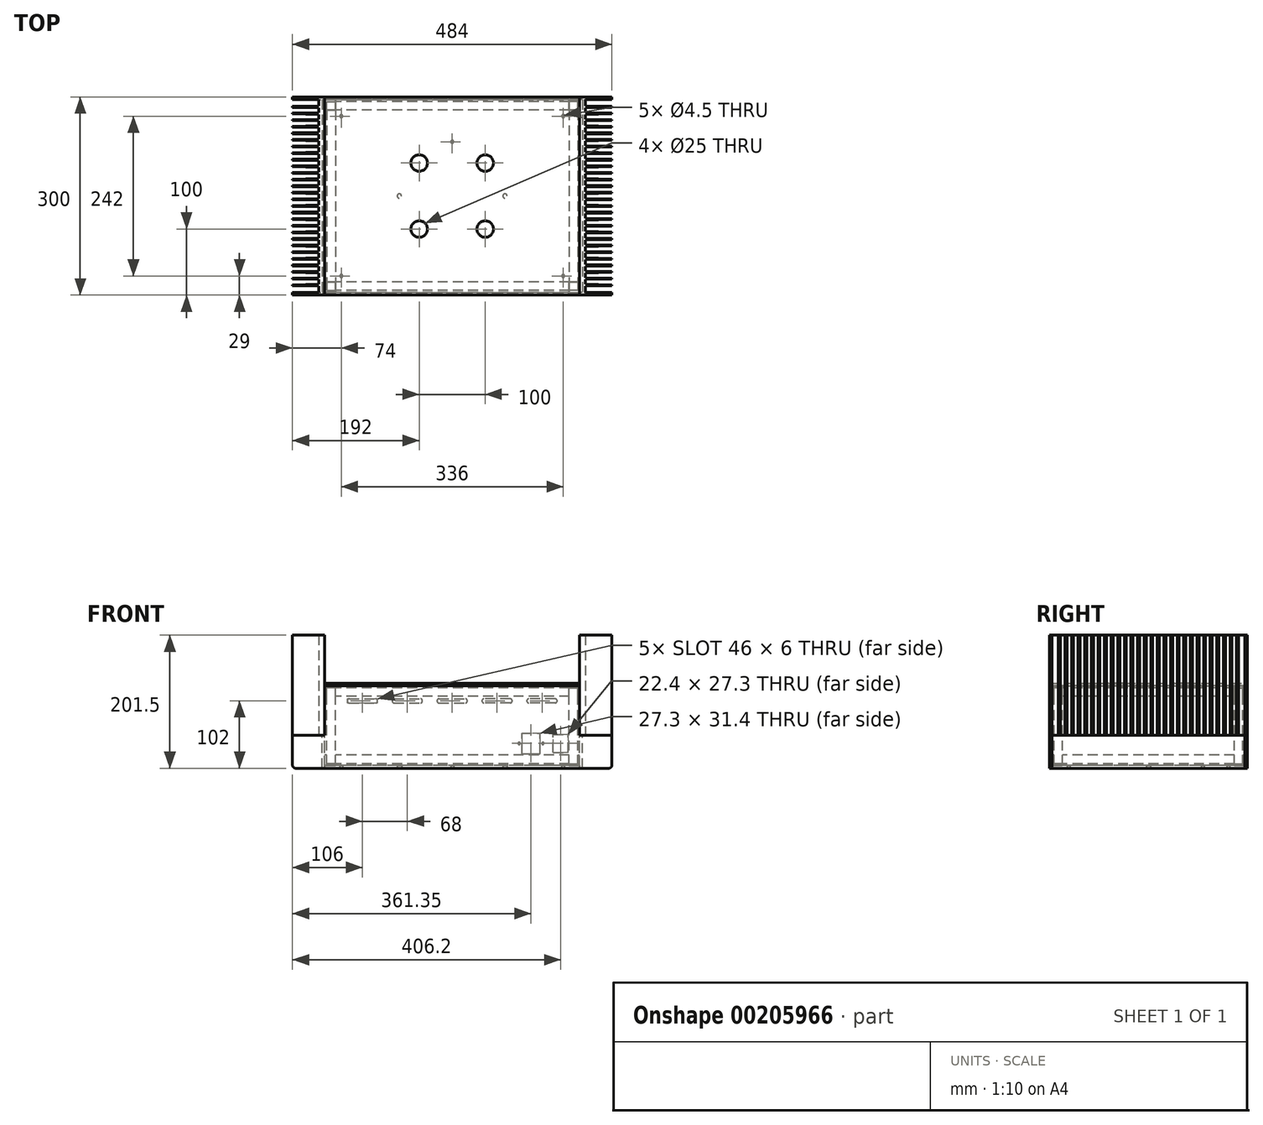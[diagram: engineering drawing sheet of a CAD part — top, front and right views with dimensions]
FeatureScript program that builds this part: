
annotation { "Feature Type Name" : "Feature", "Feature Type Description" : "" }
export const myFeature = defineFeature(function(context is Context, id is Id, definition is map)
    precondition{}
    {
        {
            var Q0;
            Q0=qCreatedBy(makeId("Top.planeOp"),FACE);
            var sketch = newSketch(context, id + "F0", { "sketchPlane" : qUnion([Q0])});
            skLineSegment(sketch, "E0", {"start": v(0, 0) * mm, "end": v(11.17, 0) * mm, "construction": true});
            skLineSegment(sketch, "E1", {"start": v(0, 0) * mm, "end": v(0, 12.82) * mm, "construction": true});
            skLineSegment(sketch, "E2", {"start": v(0, 49) * mm, "end": v(0.75, 49) * mm});
            skLineSegment(sketch, "E3", {"start": v(0.75, 49) * mm, "end": v(1.5, 9) * mm});
            skLineSegment(sketch, "E4", {"start": v(1.5, 9) * mm, "end": v(8.5, 9) * mm});
            skLineSegment(sketch, "E5", {"start": v(8.5, 9) * mm, "end": v(9.25, 49) * mm});
            skLineSegment(sketch, "E6", {"start": v(5, 24.61) * mm, "end": v(5, 0) * mm, "construction": true});
            skPoint(sketch, "E6.startSnap0", {"position": v(5, 9) * mm});
            skLineSegment(sketch, "E7", {"start": v(9.25, 49) * mm, "end": v(10, 49) * mm});
            skLineSegment(sketch, "E8.1.0.0", {"start": v(11.5, 9) * mm, "end": v(18.5, 9) * mm});
            skLineSegment(sketch, "E8.1.0.1", {"start": v(18.5, 9) * mm, "end": v(19.25, 49) * mm});
            skLineSegment(sketch, "E8.1.0.2", {"start": v(10.75, 49) * mm, "end": v(11.5, 9) * mm});
            skPoint(sketch, "E8.1.0.3", {"position": v(15, 9) * mm});
            skLineSegment(sketch, "E8.1.0.4", {"start": v(10, 49) * mm, "end": v(10.75, 49) * mm});
            skLineSegment(sketch, "E8.1.0.5", {"start": v(19.25, 49) * mm, "end": v(20, 49) * mm});
            skLineSegment(sketch, "E8.2.0.0", {"start": v(21.5, 9) * mm, "end": v(28.5, 9) * mm});
            skLineSegment(sketch, "E8.2.0.1", {"start": v(28.5, 9) * mm, "end": v(29.25, 49) * mm});
            skLineSegment(sketch, "E8.2.0.2", {"start": v(20.75, 49) * mm, "end": v(21.5, 9) * mm});
            skPoint(sketch, "E8.2.0.3", {"position": v(25, 9) * mm});
            skLineSegment(sketch, "E8.2.0.4", {"start": v(20, 49) * mm, "end": v(20.75, 49) * mm});
            skLineSegment(sketch, "E8.2.0.5", {"start": v(29.25, 49) * mm, "end": v(30, 49) * mm});
            skLineSegment(sketch, "E8.3.0.0", {"start": v(31.5, 9) * mm, "end": v(38.5, 9) * mm});
            skLineSegment(sketch, "E8.3.0.1", {"start": v(38.5, 9) * mm, "end": v(39.25, 49) * mm});
            skLineSegment(sketch, "E8.3.0.2", {"start": v(30.75, 49) * mm, "end": v(31.5, 9) * mm});
            skPoint(sketch, "E8.3.0.3", {"position": v(35, 9) * mm});
            skLineSegment(sketch, "E8.3.0.4", {"start": v(30, 49) * mm, "end": v(30.75, 49) * mm});
            skLineSegment(sketch, "E8.3.0.5", {"start": v(39.25, 49) * mm, "end": v(40, 49) * mm});
            skLineSegment(sketch, "E8.4.0.0", {"start": v(41.5, 9) * mm, "end": v(48.5, 9) * mm});
            skLineSegment(sketch, "E8.4.0.1", {"start": v(48.5, 9) * mm, "end": v(49.25, 49) * mm});
            skLineSegment(sketch, "E8.4.0.2", {"start": v(40.75, 49) * mm, "end": v(41.5, 9) * mm});
            skPoint(sketch, "E8.4.0.3", {"position": v(45, 9) * mm});
            skLineSegment(sketch, "E8.4.0.4", {"start": v(40, 49) * mm, "end": v(40.75, 49) * mm});
            skLineSegment(sketch, "E8.4.0.5", {"start": v(49.25, 49) * mm, "end": v(50, 49) * mm});
            skLineSegment(sketch, "E8.5.0.0", {"start": v(51.5, 9) * mm, "end": v(58.5, 9) * mm});
            skLineSegment(sketch, "E8.5.0.1", {"start": v(58.5, 9) * mm, "end": v(59.25, 49) * mm});
            skLineSegment(sketch, "E8.5.0.2", {"start": v(50.75, 49) * mm, "end": v(51.5, 9) * mm});
            skPoint(sketch, "E8.5.0.3", {"position": v(55, 9) * mm});
            skLineSegment(sketch, "E8.5.0.4", {"start": v(50, 49) * mm, "end": v(50.75, 49) * mm});
            skLineSegment(sketch, "E8.5.0.5", {"start": v(59.25, 49) * mm, "end": v(60, 49) * mm});
            skLineSegment(sketch, "E8.6.0.0", {"start": v(61.5, 9) * mm, "end": v(68.5, 9) * mm});
            skLineSegment(sketch, "E8.6.0.1", {"start": v(68.5, 9) * mm, "end": v(69.25, 49) * mm});
            skLineSegment(sketch, "E8.6.0.2", {"start": v(60.75, 49) * mm, "end": v(61.5, 9) * mm});
            skPoint(sketch, "E8.6.0.3", {"position": v(65, 9) * mm});
            skLineSegment(sketch, "E8.6.0.4", {"start": v(60, 49) * mm, "end": v(60.75, 49) * mm});
            skLineSegment(sketch, "E8.6.0.5", {"start": v(69.25, 49) * mm, "end": v(70, 49) * mm});
            skLineSegment(sketch, "E8.7.0.0", {"start": v(71.5, 9) * mm, "end": v(78.5, 9) * mm});
            skLineSegment(sketch, "E8.7.0.1", {"start": v(78.5, 9) * mm, "end": v(79.25, 49) * mm});
            skLineSegment(sketch, "E8.7.0.2", {"start": v(70.75, 49) * mm, "end": v(71.5, 9) * mm});
            skPoint(sketch, "E8.7.0.3", {"position": v(75, 9) * mm});
            skLineSegment(sketch, "E8.7.0.4", {"start": v(70, 49) * mm, "end": v(70.75, 49) * mm});
            skLineSegment(sketch, "E8.7.0.5", {"start": v(79.25, 49) * mm, "end": v(80, 49) * mm});
            skLineSegment(sketch, "E8.8.0.0", {"start": v(81.5, 9) * mm, "end": v(88.5, 9) * mm});
            skLineSegment(sketch, "E8.8.0.1", {"start": v(88.5, 9) * mm, "end": v(89.25, 49) * mm});
            skLineSegment(sketch, "E8.8.0.2", {"start": v(80.75, 49) * mm, "end": v(81.5, 9) * mm});
            skPoint(sketch, "E8.8.0.3", {"position": v(85, 9) * mm});
            skLineSegment(sketch, "E8.8.0.4", {"start": v(80, 49) * mm, "end": v(80.75, 49) * mm});
            skLineSegment(sketch, "E8.8.0.5", {"start": v(89.25, 49) * mm, "end": v(90, 49) * mm});
            skLineSegment(sketch, "E8.9.0.0", {"start": v(91.5, 9) * mm, "end": v(98.5, 9) * mm});
            skLineSegment(sketch, "E8.9.0.1", {"start": v(98.5, 9) * mm, "end": v(99.25, 49) * mm});
            skLineSegment(sketch, "E8.9.0.2", {"start": v(90.75, 49) * mm, "end": v(91.5, 9) * mm});
            skPoint(sketch, "E8.9.0.3", {"position": v(95, 9) * mm});
            skLineSegment(sketch, "E8.9.0.4", {"start": v(90, 49) * mm, "end": v(90.75, 49) * mm});
            skLineSegment(sketch, "E8.9.0.5", {"start": v(99.25, 49) * mm, "end": v(100, 49) * mm});
            skLineSegment(sketch, "E8.10.0.0", {"start": v(101.5, 9) * mm, "end": v(108.5, 9) * mm});
            skLineSegment(sketch, "E8.10.0.1", {"start": v(108.5, 9) * mm, "end": v(109.25, 49) * mm});
            skLineSegment(sketch, "E8.10.0.2", {"start": v(100.75, 49) * mm, "end": v(101.5, 9) * mm});
            skPoint(sketch, "E8.10.0.3", {"position": v(105, 9) * mm});
            skLineSegment(sketch, "E8.10.0.4", {"start": v(100, 49) * mm, "end": v(100.75, 49) * mm});
            skLineSegment(sketch, "E8.10.0.5", {"start": v(109.25, 49) * mm, "end": v(110, 49) * mm});
            skLineSegment(sketch, "E8.11.0.0", {"start": v(111.5, 9) * mm, "end": v(118.5, 9) * mm});
            skLineSegment(sketch, "E8.11.0.1", {"start": v(118.5, 9) * mm, "end": v(119.25, 49) * mm});
            skLineSegment(sketch, "E8.11.0.2", {"start": v(110.75, 49) * mm, "end": v(111.5, 9) * mm});
            skPoint(sketch, "E8.11.0.3", {"position": v(115, 9) * mm});
            skLineSegment(sketch, "E8.11.0.4", {"start": v(110, 49) * mm, "end": v(110.75, 49) * mm});
            skLineSegment(sketch, "E8.11.0.5", {"start": v(119.25, 49) * mm, "end": v(120, 49) * mm});
            skLineSegment(sketch, "E8.12.0.0", {"start": v(121.5, 9) * mm, "end": v(128.5, 9) * mm});
            skLineSegment(sketch, "E8.12.0.1", {"start": v(128.5, 9) * mm, "end": v(129.25, 49) * mm});
            skLineSegment(sketch, "E8.12.0.2", {"start": v(120.75, 49) * mm, "end": v(121.5, 9) * mm});
            skPoint(sketch, "E8.12.0.3", {"position": v(125, 9) * mm});
            skLineSegment(sketch, "E8.12.0.4", {"start": v(120, 49) * mm, "end": v(120.75, 49) * mm});
            skLineSegment(sketch, "E8.12.0.5", {"start": v(129.25, 49) * mm, "end": v(130, 49) * mm});
            skLineSegment(sketch, "E8.13.0.0", {"start": v(131.5, 9) * mm, "end": v(138.5, 9) * mm});
            skLineSegment(sketch, "E8.13.0.1", {"start": v(138.5, 9) * mm, "end": v(139.25, 49) * mm});
            skLineSegment(sketch, "E8.13.0.2", {"start": v(130.75, 49) * mm, "end": v(131.5, 9) * mm});
            skPoint(sketch, "E8.13.0.3", {"position": v(135, 9) * mm});
            skLineSegment(sketch, "E8.13.0.4", {"start": v(130, 49) * mm, "end": v(130.75, 49) * mm});
            skLineSegment(sketch, "E8.13.0.5", {"start": v(139.25, 49) * mm, "end": v(140, 49) * mm});
            skLineSegment(sketch, "E8.14.0.2", {"start": v(140.75, 49) * mm, "end": v(141.5, 9) * mm});
            skLineSegment(sketch, "E8.14.0.4", {"start": v(140, 49) * mm, "end": v(140.75, 49) * mm});
            skLineSegment(sketch, "E8.direction1", {"start": v(1.5, 9) * mm, "end": v(11.5, 9) * mm, "construction": true});
            skLineSegment(sketch, "E9.1.0.0", {"start": v(-9.25, 49) * mm, "end": v(-8.5, 9) * mm});
            skLineSegment(sketch, "E9.1.0.1", {"start": v(-8.5, 9) * mm, "end": v(-1.5, 9) * mm});
            skLineSegment(sketch, "E9.1.0.2", {"start": v(-1.5, 9) * mm, "end": v(-0.75, 49) * mm});
            skPoint(sketch, "E9.1.0.3", {"position": v(-5, 9) * mm});
            skLineSegment(sketch, "E9.1.0.4", {"start": v(-10, 49) * mm, "end": v(-9.25, 49) * mm});
            skLineSegment(sketch, "E9.1.0.5", {"start": v(-0.75, 49) * mm, "end": v(0, 49) * mm});
            skLineSegment(sketch, "E9.2.0.0", {"start": v(-19.25, 49) * mm, "end": v(-18.5, 9) * mm});
            skLineSegment(sketch, "E9.2.0.1", {"start": v(-18.5, 9) * mm, "end": v(-11.5, 9) * mm});
            skLineSegment(sketch, "E9.2.0.2", {"start": v(-11.5, 9) * mm, "end": v(-10.75, 49) * mm});
            skPoint(sketch, "E9.2.0.3", {"position": v(-15, 9) * mm});
            skLineSegment(sketch, "E9.2.0.4", {"start": v(-20, 49) * mm, "end": v(-19.25, 49) * mm});
            skLineSegment(sketch, "E9.2.0.5", {"start": v(-10.75, 49) * mm, "end": v(-10, 49) * mm});
            skLineSegment(sketch, "E9.direction1", {"start": v(-8.5, 9) * mm, "end": v(1.5, 9) * mm, "construction": true});
            skLineSegment(sketch, "E10.0.3.0", {"start": v(-29.25, 49) * mm, "end": v(-28.5, 9) * mm});
            skLineSegment(sketch, "E10.3.3.0", {"start": v(-28.5, 9) * mm, "end": v(-21.5, 9) * mm});
            skLineSegment(sketch, "E10.6.3.0", {"start": v(-21.5, 9) * mm, "end": v(-20.75, 49) * mm});
            skPoint(sketch, "E10.9.3.0", {"position": v(-25, 9) * mm});
            skLineSegment(sketch, "E10.10.3.0", {"start": v(-30, 49) * mm, "end": v(-29.25, 49) * mm});
            skLineSegment(sketch, "E10.13.3.0", {"start": v(-20.75, 49) * mm, "end": v(-20, 49) * mm});
            skLineSegment(sketch, "E10.0.4.0", {"start": v(-39.25, 49) * mm, "end": v(-38.5, 9) * mm});
            skLineSegment(sketch, "E10.3.4.0", {"start": v(-38.5, 9) * mm, "end": v(-31.5, 9) * mm});
            skLineSegment(sketch, "E10.6.4.0", {"start": v(-31.5, 9) * mm, "end": v(-30.75, 49) * mm});
            skPoint(sketch, "E10.9.4.0", {"position": v(-35, 9) * mm});
            skLineSegment(sketch, "E10.10.4.0", {"start": v(-40, 49) * mm, "end": v(-39.25, 49) * mm});
            skLineSegment(sketch, "E10.13.4.0", {"start": v(-30.75, 49) * mm, "end": v(-30, 49) * mm});
            skLineSegment(sketch, "E10.0.5.0", {"start": v(-49.25, 49) * mm, "end": v(-48.5, 9) * mm});
            skLineSegment(sketch, "E10.3.5.0", {"start": v(-48.5, 9) * mm, "end": v(-41.5, 9) * mm});
            skLineSegment(sketch, "E10.6.5.0", {"start": v(-41.5, 9) * mm, "end": v(-40.75, 49) * mm});
            skPoint(sketch, "E10.9.5.0", {"position": v(-45, 9) * mm});
            skLineSegment(sketch, "E10.10.5.0", {"start": v(-50, 49) * mm, "end": v(-49.25, 49) * mm});
            skLineSegment(sketch, "E10.13.5.0", {"start": v(-40.75, 49) * mm, "end": v(-40, 49) * mm});
            skLineSegment(sketch, "E10.0.6.0", {"start": v(-59.25, 49) * mm, "end": v(-58.5, 9) * mm});
            skLineSegment(sketch, "E10.3.6.0", {"start": v(-58.5, 9) * mm, "end": v(-51.5, 9) * mm});
            skLineSegment(sketch, "E10.6.6.0", {"start": v(-51.5, 9) * mm, "end": v(-50.75, 49) * mm});
            skPoint(sketch, "E10.9.6.0", {"position": v(-55, 9) * mm});
            skLineSegment(sketch, "E10.10.6.0", {"start": v(-60, 49) * mm, "end": v(-59.25, 49) * mm});
            skLineSegment(sketch, "E10.13.6.0", {"start": v(-50.75, 49) * mm, "end": v(-50, 49) * mm});
            skLineSegment(sketch, "E10.0.7.0", {"start": v(-69.25, 49) * mm, "end": v(-68.5, 9) * mm});
            skLineSegment(sketch, "E10.3.7.0", {"start": v(-68.5, 9) * mm, "end": v(-61.5, 9) * mm});
            skLineSegment(sketch, "E10.6.7.0", {"start": v(-61.5, 9) * mm, "end": v(-60.75, 49) * mm});
            skPoint(sketch, "E10.9.7.0", {"position": v(-65, 9) * mm});
            skLineSegment(sketch, "E10.10.7.0", {"start": v(-70, 49) * mm, "end": v(-69.25, 49) * mm});
            skLineSegment(sketch, "E10.13.7.0", {"start": v(-60.75, 49) * mm, "end": v(-60, 49) * mm});
            skLineSegment(sketch, "E10.0.8.0", {"start": v(-79.25, 49) * mm, "end": v(-78.5, 9) * mm});
            skLineSegment(sketch, "E10.3.8.0", {"start": v(-78.5, 9) * mm, "end": v(-71.5, 9) * mm});
            skLineSegment(sketch, "E10.6.8.0", {"start": v(-71.5, 9) * mm, "end": v(-70.75, 49) * mm});
            skPoint(sketch, "E10.9.8.0", {"position": v(-75, 9) * mm});
            skLineSegment(sketch, "E10.10.8.0", {"start": v(-80, 49) * mm, "end": v(-79.25, 49) * mm});
            skLineSegment(sketch, "E10.13.8.0", {"start": v(-70.75, 49) * mm, "end": v(-70, 49) * mm});
            skLineSegment(sketch, "E10.0.9.0", {"start": v(-89.25, 49) * mm, "end": v(-88.5, 9) * mm});
            skLineSegment(sketch, "E10.3.9.0", {"start": v(-88.5, 9) * mm, "end": v(-81.5, 9) * mm});
            skLineSegment(sketch, "E10.6.9.0", {"start": v(-81.5, 9) * mm, "end": v(-80.75, 49) * mm});
            skPoint(sketch, "E10.9.9.0", {"position": v(-85, 9) * mm});
            skLineSegment(sketch, "E10.10.9.0", {"start": v(-90, 49) * mm, "end": v(-89.25, 49) * mm});
            skLineSegment(sketch, "E10.13.9.0", {"start": v(-80.75, 49) * mm, "end": v(-80, 49) * mm});
            skLineSegment(sketch, "E10.0.10.0", {"start": v(-99.25, 49) * mm, "end": v(-98.5, 9) * mm});
            skLineSegment(sketch, "E10.3.10.0", {"start": v(-98.5, 9) * mm, "end": v(-91.5, 9) * mm});
            skLineSegment(sketch, "E10.6.10.0", {"start": v(-91.5, 9) * mm, "end": v(-90.75, 49) * mm});
            skPoint(sketch, "E10.9.10.0", {"position": v(-95, 9) * mm});
            skLineSegment(sketch, "E10.10.10.0", {"start": v(-100, 49) * mm, "end": v(-99.25, 49) * mm});
            skLineSegment(sketch, "E10.13.10.0", {"start": v(-90.75, 49) * mm, "end": v(-90, 49) * mm});
            skLineSegment(sketch, "E10.0.11.0", {"start": v(-109.25, 49) * mm, "end": v(-108.5, 9) * mm});
            skLineSegment(sketch, "E10.3.11.0", {"start": v(-108.5, 9) * mm, "end": v(-101.5, 9) * mm});
            skLineSegment(sketch, "E10.6.11.0", {"start": v(-101.5, 9) * mm, "end": v(-100.75, 49) * mm});
            skPoint(sketch, "E10.9.11.0", {"position": v(-105, 9) * mm});
            skLineSegment(sketch, "E10.10.11.0", {"start": v(-110, 49) * mm, "end": v(-109.25, 49) * mm});
            skLineSegment(sketch, "E10.13.11.0", {"start": v(-100.75, 49) * mm, "end": v(-100, 49) * mm});
            skLineSegment(sketch, "E10.0.12.0", {"start": v(-119.25, 49) * mm, "end": v(-118.5, 9) * mm});
            skLineSegment(sketch, "E10.3.12.0", {"start": v(-118.5, 9) * mm, "end": v(-111.5, 9) * mm});
            skLineSegment(sketch, "E10.6.12.0", {"start": v(-111.5, 9) * mm, "end": v(-110.75, 49) * mm});
            skPoint(sketch, "E10.9.12.0", {"position": v(-115, 9) * mm});
            skLineSegment(sketch, "E10.10.12.0", {"start": v(-120, 49) * mm, "end": v(-119.25, 49) * mm});
            skLineSegment(sketch, "E10.13.12.0", {"start": v(-110.75, 49) * mm, "end": v(-110, 49) * mm});
            skLineSegment(sketch, "E10.0.13.0", {"start": v(-129.25, 49) * mm, "end": v(-128.5, 9) * mm});
            skLineSegment(sketch, "E10.3.13.0", {"start": v(-128.5, 9) * mm, "end": v(-121.5, 9) * mm});
            skLineSegment(sketch, "E10.6.13.0", {"start": v(-121.5, 9) * mm, "end": v(-120.75, 49) * mm});
            skPoint(sketch, "E10.9.13.0", {"position": v(-125, 9) * mm});
            skLineSegment(sketch, "E10.10.13.0", {"start": v(-130, 49) * mm, "end": v(-129.25, 49) * mm});
            skLineSegment(sketch, "E10.13.13.0", {"start": v(-120.75, 49) * mm, "end": v(-120, 49) * mm});
            skLineSegment(sketch, "E10.6.14.0", {"start": v(-131.5, 9) * mm, "end": v(-130.75, 49) * mm});
            skLineSegment(sketch, "E10.13.14.0", {"start": v(-130.75, 49) * mm, "end": v(-130, 49) * mm});
            skLineSegment(sketch, "E11", {"start": v(-141, 49) * mm, "end": v(-145, 49) * mm});
            skLineSegment(sketch, "E12", {"start": v(-145, 49) * mm, "end": v(-145, 0) * mm});
            skLineSegment(sketch, "E13", {"start": v(-145, 0) * mm, "end": v(155, 0) * mm});
            skLineSegment(sketch, "E14", {"start": v(155, 0) * mm, "end": v(155, 49) * mm});
            skLineSegment(sketch, "E15", {"start": v(155, 49) * mm, "end": v(151, 49) * mm});
            skLineSegment(sketch, "E16", {"start": v(-141, 49) * mm, "end": v(-141, 9) * mm});
            skLineSegment(sketch, "E17", {"start": v(151, 49) * mm, "end": v(151, 9) * mm});
            skLineSegment(sketch, "E18", {"start": v(141.5, 9) * mm, "end": v(151, 9) * mm});
            skLineSegment(sketch, "E19", {"start": v(-131.5, 9) * mm, "end": v(-141, 9) * mm});
            skSolve(sketch);
        }
        {
            var Q0;
            Q0=qSketchRegion(id+"F0",true);
            extrude(context, id + "F1", {"entities" : qUnion([Q0]), "depth" : 151.5 * mm});
        }
        {
            var Q0;
            Q0=qCreatedBy(makeId("Front.planeOp"),FACE);
            var sketch = newSketch(context, id + "F2", { "sketchPlane" : qUnion([Q0])});
            skLineSegment(sketch, "E20.bottom", {"start": v(0, 0) * mm, "end": v(0, 0) * mm});
            skLineSegment(sketch, "E20.top", {"start": v(0, 73.55) * mm, "end": v(0, 73.55) * mm});
            skLineSegment(sketch, "E20.left", {"start": v(0, 0) * mm, "end": v(0, 73.55) * mm, "construction": true});
            skLineSegment(sketch, "E20.right", {"start": v(0, 0) * mm, "end": v(0, 73.55) * mm, "construction": true});
            skSolve(sketch);
        }
        {
            var Q0;
            Q0=makeQuery(id+"F1.opExtrude","SWEPT_BODY",BODY,{"disambiguationData":[OSD([sQuery(id+"F0.wireOp",EDGE,"E2"),sQuery(id+"F0.wireOp",EDGE,"E3"),sQuery(id+"F0.wireOp",EDGE,"E4"),sQuery(id+"F0.wireOp",EDGE,"E5"),sQuery(id+"F0.wireOp",EDGE,"E7"),sQuery(id+"F0.wireOp",EDGE,"E8.1.0.0"),sQuery(id+"F0.wireOp",EDGE,"E8.1.0.1"),sQuery(id+"F0.wireOp",EDGE,"E8.1.0.2"),sQuery(id+"F0.wireOp",EDGE,"E8.1.0.4"),sQuery(id+"F0.wireOp",EDGE,"E8.1.0.5"),sQuery(id+"F0.wireOp",EDGE,"E8.2.0.0"),sQuery(id+"F0.wireOp",EDGE,"E8.2.0.1"),sQuery(id+"F0.wireOp",EDGE,"E8.2.0.2"),sQuery(id+"F0.wireOp",EDGE,"E8.2.0.4"),sQuery(id+"F0.wireOp",EDGE,"E8.2.0.5"),sQuery(id+"F0.wireOp",EDGE,"E8.3.0.0"),sQuery(id+"F0.wireOp",EDGE,"E8.3.0.1"),sQuery(id+"F0.wireOp",EDGE,"E8.3.0.2"),sQuery(id+"F0.wireOp",EDGE,"E8.3.0.4"),sQuery(id+"F0.wireOp",EDGE,"E8.3.0.5"),sQuery(id+"F0.wireOp",EDGE,"E8.4.0.0"),sQuery(id+"F0.wireOp",EDGE,"E8.4.0.1"),sQuery(id+"F0.wireOp",EDGE,"E8.4.0.2"),sQuery(id+"F0.wireOp",EDGE,"E8.4.0.4"),sQuery(id+"F0.wireOp",EDGE,"E8.4.0.5"),sQuery(id+"F0.wireOp",EDGE,"E8.5.0.0"),sQuery(id+"F0.wireOp",EDGE,"E8.5.0.1"),sQuery(id+"F0.wireOp",EDGE,"E8.5.0.2"),sQuery(id+"F0.wireOp",EDGE,"E8.5.0.4"),sQuery(id+"F0.wireOp",EDGE,"E8.5.0.5"),sQuery(id+"F0.wireOp",EDGE,"E8.6.0.0"),sQuery(id+"F0.wireOp",EDGE,"E8.6.0.1"),sQuery(id+"F0.wireOp",EDGE,"E8.6.0.2"),sQuery(id+"F0.wireOp",EDGE,"E8.6.0.4"),sQuery(id+"F0.wireOp",EDGE,"E8.6.0.5"),sQuery(id+"F0.wireOp",EDGE,"E8.7.0.0"),sQuery(id+"F0.wireOp",EDGE,"E8.7.0.1"),sQuery(id+"F0.wireOp",EDGE,"E8.7.0.2"),sQuery(id+"F0.wireOp",EDGE,"E8.7.0.4"),sQuery(id+"F0.wireOp",EDGE,"E8.7.0.5"),sQuery(id+"F0.wireOp",EDGE,"E8.8.0.0"),sQuery(id+"F0.wireOp",EDGE,"E8.8.0.1"),sQuery(id+"F0.wireOp",EDGE,"E8.8.0.2"),sQuery(id+"F0.wireOp",EDGE,"E8.8.0.4"),sQuery(id+"F0.wireOp",EDGE,"E8.8.0.5"),sQuery(id+"F0.wireOp",EDGE,"E8.9.0.0"),sQuery(id+"F0.wireOp",EDGE,"E8.9.0.1"),sQuery(id+"F0.wireOp",EDGE,"E8.9.0.2"),sQuery(id+"F0.wireOp",EDGE,"E8.9.0.4"),sQuery(id+"F0.wireOp",EDGE,"E8.9.0.5"),sQuery(id+"F0.wireOp",EDGE,"E8.10.0.0"),sQuery(id+"F0.wireOp",EDGE,"E8.10.0.1"),sQuery(id+"F0.wireOp",EDGE,"E8.10.0.2"),sQuery(id+"F0.wireOp",EDGE,"E8.10.0.4"),sQuery(id+"F0.wireOp",EDGE,"E8.10.0.5"),sQuery(id+"F0.wireOp",EDGE,"E8.11.0.0"),sQuery(id+"F0.wireOp",EDGE,"E8.11.0.1"),sQuery(id+"F0.wireOp",EDGE,"E8.11.0.2"),sQuery(id+"F0.wireOp",EDGE,"E8.11.0.4"),sQuery(id+"F0.wireOp",EDGE,"E8.11.0.5"),sQuery(id+"F0.wireOp",EDGE,"E8.12.0.0"),sQuery(id+"F0.wireOp",EDGE,"E8.12.0.1"),sQuery(id+"F0.wireOp",EDGE,"E8.12.0.2"),sQuery(id+"F0.wireOp",EDGE,"E8.12.0.4"),sQuery(id+"F0.wireOp",EDGE,"E8.12.0.5"),sQuery(id+"F0.wireOp",EDGE,"E8.13.0.0"),sQuery(id+"F0.wireOp",EDGE,"E8.13.0.1"),sQuery(id+"F0.wireOp",EDGE,"E8.13.0.2"),sQuery(id+"F0.wireOp",EDGE,"E8.13.0.4"),sQuery(id+"F0.wireOp",EDGE,"E8.13.0.5"),sQuery(id+"F0.wireOp",EDGE,"E8.14.0.0"),sQuery(id+"F0.wireOp",EDGE,"E8.14.0.1"),sQuery(id+"F0.wireOp",EDGE,"E8.14.0.2"),sQuery(id+"F0.wireOp",EDGE,"E8.14.0.4"),sQuery(id+"F0.wireOp",EDGE,"E8.14.0.5"),sQuery(id+"F0.wireOp",EDGE,"E9.1.0.0"),sQuery(id+"F0.wireOp",EDGE,"E9.1.0.1"),sQuery(id+"F0.wireOp",EDGE,"E9.1.0.2"),sQuery(id+"F0.wireOp",EDGE,"E9.1.0.4"),sQuery(id+"F0.wireOp",EDGE,"E9.1.0.5"),sQuery(id+"F0.wireOp",EDGE,"E9.2.0.0"),sQuery(id+"F0.wireOp",EDGE,"E9.2.0.1"),sQuery(id+"F0.wireOp",EDGE,"E9.2.0.2"),sQuery(id+"F0.wireOp",EDGE,"E9.2.0.4"),sQuery(id+"F0.wireOp",EDGE,"E9.2.0.5"),sQuery(id+"F0.wireOp",EDGE,"E10.0.3.0"),sQuery(id+"F0.wireOp",EDGE,"E10.3.3.0"),sQuery(id+"F0.wireOp",EDGE,"E10.6.3.0"),sQuery(id+"F0.wireOp",EDGE,"E10.10.3.0"),sQuery(id+"F0.wireOp",EDGE,"E10.13.3.0"),sQuery(id+"F0.wireOp",EDGE,"E10.0.4.0"),sQuery(id+"F0.wireOp",EDGE,"E10.3.4.0"),sQuery(id+"F0.wireOp",EDGE,"E10.6.4.0"),sQuery(id+"F0.wireOp",EDGE,"E10.10.4.0"),sQuery(id+"F0.wireOp",EDGE,"E10.13.4.0"),sQuery(id+"F0.wireOp",EDGE,"E10.0.5.0"),sQuery(id+"F0.wireOp",EDGE,"E10.3.5.0"),sQuery(id+"F0.wireOp",EDGE,"E10.6.5.0"),sQuery(id+"F0.wireOp",EDGE,"E10.10.5.0"),sQuery(id+"F0.wireOp",EDGE,"E10.13.5.0"),sQuery(id+"F0.wireOp",EDGE,"E10.0.6.0"),sQuery(id+"F0.wireOp",EDGE,"E10.3.6.0"),sQuery(id+"F0.wireOp",EDGE,"E10.6.6.0"),sQuery(id+"F0.wireOp",EDGE,"E10.10.6.0"),sQuery(id+"F0.wireOp",EDGE,"E10.13.6.0"),sQuery(id+"F0.wireOp",EDGE,"E10.0.7.0"),sQuery(id+"F0.wireOp",EDGE,"E10.3.7.0"),sQuery(id+"F0.wireOp",EDGE,"E10.6.7.0"),sQuery(id+"F0.wireOp",EDGE,"E10.10.7.0"),sQuery(id+"F0.wireOp",EDGE,"E10.13.7.0"),sQuery(id+"F0.wireOp",EDGE,"E10.0.8.0"),sQuery(id+"F0.wireOp",EDGE,"E10.3.8.0"),sQuery(id+"F0.wireOp",EDGE,"E10.6.8.0"),sQuery(id+"F0.wireOp",EDGE,"E10.10.8.0"),sQuery(id+"F0.wireOp",EDGE,"E10.13.8.0"),sQuery(id+"F0.wireOp",EDGE,"E10.0.9.0"),sQuery(id+"F0.wireOp",EDGE,"E10.3.9.0"),sQuery(id+"F0.wireOp",EDGE,"E10.6.9.0"),sQuery(id+"F0.wireOp",EDGE,"E10.10.9.0"),sQuery(id+"F0.wireOp",EDGE,"E10.13.9.0"),sQuery(id+"F0.wireOp",EDGE,"E10.0.10.0"),sQuery(id+"F0.wireOp",EDGE,"E10.3.10.0"),sQuery(id+"F0.wireOp",EDGE,"E10.6.10.0"),sQuery(id+"F0.wireOp",EDGE,"E10.10.10.0"),sQuery(id+"F0.wireOp",EDGE,"E10.13.10.0"),sQuery(id+"F0.wireOp",EDGE,"E10.0.11.0"),sQuery(id+"F0.wireOp",EDGE,"E10.3.11.0"),sQuery(id+"F0.wireOp",EDGE,"E10.6.11.0"),sQuery(id+"F0.wireOp",EDGE,"E10.10.11.0"),sQuery(id+"F0.wireOp",EDGE,"E10.13.11.0"),sQuery(id+"F0.wireOp",EDGE,"E10.0.12.0"),sQuery(id+"F0.wireOp",EDGE,"E10.3.12.0"),sQuery(id+"F0.wireOp",EDGE,"E10.6.12.0"),sQuery(id+"F0.wireOp",EDGE,"E10.10.12.0"),sQuery(id+"F0.wireOp",EDGE,"E10.13.12.0"),sQuery(id+"F0.wireOp",EDGE,"E10.0.13.0"),sQuery(id+"F0.wireOp",EDGE,"E10.3.13.0"),sQuery(id+"F0.wireOp",EDGE,"E10.6.13.0"),sQuery(id+"F0.wireOp",EDGE,"E10.10.13.0"),sQuery(id+"F0.wireOp",EDGE,"E10.13.13.0"),sQuery(id+"F0.wireOp",EDGE,"E10.0.14.0"),sQuery(id+"F0.wireOp",EDGE,"E10.3.14.0"),sQuery(id+"F0.wireOp",EDGE,"E10.6.14.0"),sQuery(id+"F0.wireOp",EDGE,"E10.10.14.0"),sQuery(id+"F0.wireOp",EDGE,"E10.13.14.0"),sQuery(id+"F0.wireOp",EDGE,"E11"),sQuery(id+"F0.wireOp",EDGE,"E12"),sQuery(id+"F0.wireOp",EDGE,"E13"),sQuery(id+"F0.wireOp",EDGE,"E14"),sQuery(id+"F0.wireOp",EDGE,"E15")])]});
            var Q1;
            Q1=sQuery(id+"F2.wireOp",EDGE,"E20.right");
            transform(context, id + "F3", {"entities" : qUnion([Q0]), "transformType" : TransformType.ROTATION, "transformAxis" : qUnion([Q1]), "angle" : 90 * degree, "makeCopy" : false});
        }
        {
            var Q0;
            Q0=makeQuery(id+"F1.opExtrude","SWEPT_BODY",BODY,{"disambiguationData":[OSD([sQuery(id+"F0.wireOp",EDGE,"E2"),sQuery(id+"F0.wireOp",EDGE,"E3"),sQuery(id+"F0.wireOp",EDGE,"E4"),sQuery(id+"F0.wireOp",EDGE,"E5"),sQuery(id+"F0.wireOp",EDGE,"E7"),sQuery(id+"F0.wireOp",EDGE,"E8.1.0.0"),sQuery(id+"F0.wireOp",EDGE,"E8.1.0.1"),sQuery(id+"F0.wireOp",EDGE,"E8.1.0.2"),sQuery(id+"F0.wireOp",EDGE,"E8.1.0.4"),sQuery(id+"F0.wireOp",EDGE,"E8.1.0.5"),sQuery(id+"F0.wireOp",EDGE,"E8.2.0.0"),sQuery(id+"F0.wireOp",EDGE,"E8.2.0.1"),sQuery(id+"F0.wireOp",EDGE,"E8.2.0.2"),sQuery(id+"F0.wireOp",EDGE,"E8.2.0.4"),sQuery(id+"F0.wireOp",EDGE,"E8.2.0.5"),sQuery(id+"F0.wireOp",EDGE,"E8.3.0.0"),sQuery(id+"F0.wireOp",EDGE,"E8.3.0.1"),sQuery(id+"F0.wireOp",EDGE,"E8.3.0.2"),sQuery(id+"F0.wireOp",EDGE,"E8.3.0.4"),sQuery(id+"F0.wireOp",EDGE,"E8.3.0.5"),sQuery(id+"F0.wireOp",EDGE,"E8.4.0.0"),sQuery(id+"F0.wireOp",EDGE,"E8.4.0.1"),sQuery(id+"F0.wireOp",EDGE,"E8.4.0.2"),sQuery(id+"F0.wireOp",EDGE,"E8.4.0.4"),sQuery(id+"F0.wireOp",EDGE,"E8.4.0.5"),sQuery(id+"F0.wireOp",EDGE,"E8.5.0.0"),sQuery(id+"F0.wireOp",EDGE,"E8.5.0.1"),sQuery(id+"F0.wireOp",EDGE,"E8.5.0.2"),sQuery(id+"F0.wireOp",EDGE,"E8.5.0.4"),sQuery(id+"F0.wireOp",EDGE,"E8.5.0.5"),sQuery(id+"F0.wireOp",EDGE,"E8.6.0.0"),sQuery(id+"F0.wireOp",EDGE,"E8.6.0.1"),sQuery(id+"F0.wireOp",EDGE,"E8.6.0.2"),sQuery(id+"F0.wireOp",EDGE,"E8.6.0.4"),sQuery(id+"F0.wireOp",EDGE,"E8.6.0.5"),sQuery(id+"F0.wireOp",EDGE,"E8.7.0.0"),sQuery(id+"F0.wireOp",EDGE,"E8.7.0.1"),sQuery(id+"F0.wireOp",EDGE,"E8.7.0.2"),sQuery(id+"F0.wireOp",EDGE,"E8.7.0.4"),sQuery(id+"F0.wireOp",EDGE,"E8.7.0.5"),sQuery(id+"F0.wireOp",EDGE,"E8.8.0.0"),sQuery(id+"F0.wireOp",EDGE,"E8.8.0.1"),sQuery(id+"F0.wireOp",EDGE,"E8.8.0.2"),sQuery(id+"F0.wireOp",EDGE,"E8.8.0.4"),sQuery(id+"F0.wireOp",EDGE,"E8.8.0.5"),sQuery(id+"F0.wireOp",EDGE,"E8.9.0.0"),sQuery(id+"F0.wireOp",EDGE,"E8.9.0.1"),sQuery(id+"F0.wireOp",EDGE,"E8.9.0.2"),sQuery(id+"F0.wireOp",EDGE,"E8.9.0.4"),sQuery(id+"F0.wireOp",EDGE,"E8.9.0.5"),sQuery(id+"F0.wireOp",EDGE,"E8.10.0.0"),sQuery(id+"F0.wireOp",EDGE,"E8.10.0.1"),sQuery(id+"F0.wireOp",EDGE,"E8.10.0.2"),sQuery(id+"F0.wireOp",EDGE,"E8.10.0.4"),sQuery(id+"F0.wireOp",EDGE,"E8.10.0.5"),sQuery(id+"F0.wireOp",EDGE,"E8.11.0.0"),sQuery(id+"F0.wireOp",EDGE,"E8.11.0.1"),sQuery(id+"F0.wireOp",EDGE,"E8.11.0.2"),sQuery(id+"F0.wireOp",EDGE,"E8.11.0.4"),sQuery(id+"F0.wireOp",EDGE,"E8.11.0.5"),sQuery(id+"F0.wireOp",EDGE,"E8.12.0.0"),sQuery(id+"F0.wireOp",EDGE,"E8.12.0.1"),sQuery(id+"F0.wireOp",EDGE,"E8.12.0.2"),sQuery(id+"F0.wireOp",EDGE,"E8.12.0.4"),sQuery(id+"F0.wireOp",EDGE,"E8.12.0.5"),sQuery(id+"F0.wireOp",EDGE,"E8.13.0.0"),sQuery(id+"F0.wireOp",EDGE,"E8.13.0.1"),sQuery(id+"F0.wireOp",EDGE,"E8.13.0.2"),sQuery(id+"F0.wireOp",EDGE,"E8.13.0.4"),sQuery(id+"F0.wireOp",EDGE,"E8.13.0.5"),sQuery(id+"F0.wireOp",EDGE,"E8.14.0.0"),sQuery(id+"F0.wireOp",EDGE,"E8.14.0.1"),sQuery(id+"F0.wireOp",EDGE,"E8.14.0.2"),sQuery(id+"F0.wireOp",EDGE,"E8.14.0.4"),sQuery(id+"F0.wireOp",EDGE,"E8.14.0.5"),sQuery(id+"F0.wireOp",EDGE,"E9.1.0.0"),sQuery(id+"F0.wireOp",EDGE,"E9.1.0.1"),sQuery(id+"F0.wireOp",EDGE,"E9.1.0.2"),sQuery(id+"F0.wireOp",EDGE,"E9.1.0.4"),sQuery(id+"F0.wireOp",EDGE,"E9.1.0.5"),sQuery(id+"F0.wireOp",EDGE,"E9.2.0.0"),sQuery(id+"F0.wireOp",EDGE,"E9.2.0.1"),sQuery(id+"F0.wireOp",EDGE,"E9.2.0.2"),sQuery(id+"F0.wireOp",EDGE,"E9.2.0.4"),sQuery(id+"F0.wireOp",EDGE,"E9.2.0.5"),sQuery(id+"F0.wireOp",EDGE,"E10.0.3.0"),sQuery(id+"F0.wireOp",EDGE,"E10.3.3.0"),sQuery(id+"F0.wireOp",EDGE,"E10.6.3.0"),sQuery(id+"F0.wireOp",EDGE,"E10.10.3.0"),sQuery(id+"F0.wireOp",EDGE,"E10.13.3.0"),sQuery(id+"F0.wireOp",EDGE,"E10.0.4.0"),sQuery(id+"F0.wireOp",EDGE,"E10.3.4.0"),sQuery(id+"F0.wireOp",EDGE,"E10.6.4.0"),sQuery(id+"F0.wireOp",EDGE,"E10.10.4.0"),sQuery(id+"F0.wireOp",EDGE,"E10.13.4.0"),sQuery(id+"F0.wireOp",EDGE,"E10.0.5.0"),sQuery(id+"F0.wireOp",EDGE,"E10.3.5.0"),sQuery(id+"F0.wireOp",EDGE,"E10.6.5.0"),sQuery(id+"F0.wireOp",EDGE,"E10.10.5.0"),sQuery(id+"F0.wireOp",EDGE,"E10.13.5.0"),sQuery(id+"F0.wireOp",EDGE,"E10.0.6.0"),sQuery(id+"F0.wireOp",EDGE,"E10.3.6.0"),sQuery(id+"F0.wireOp",EDGE,"E10.6.6.0"),sQuery(id+"F0.wireOp",EDGE,"E10.10.6.0"),sQuery(id+"F0.wireOp",EDGE,"E10.13.6.0"),sQuery(id+"F0.wireOp",EDGE,"E10.0.7.0"),sQuery(id+"F0.wireOp",EDGE,"E10.3.7.0"),sQuery(id+"F0.wireOp",EDGE,"E10.6.7.0"),sQuery(id+"F0.wireOp",EDGE,"E10.10.7.0"),sQuery(id+"F0.wireOp",EDGE,"E10.13.7.0"),sQuery(id+"F0.wireOp",EDGE,"E10.0.8.0"),sQuery(id+"F0.wireOp",EDGE,"E10.3.8.0"),sQuery(id+"F0.wireOp",EDGE,"E10.6.8.0"),sQuery(id+"F0.wireOp",EDGE,"E10.10.8.0"),sQuery(id+"F0.wireOp",EDGE,"E10.13.8.0"),sQuery(id+"F0.wireOp",EDGE,"E10.0.9.0"),sQuery(id+"F0.wireOp",EDGE,"E10.3.9.0"),sQuery(id+"F0.wireOp",EDGE,"E10.6.9.0"),sQuery(id+"F0.wireOp",EDGE,"E10.10.9.0"),sQuery(id+"F0.wireOp",EDGE,"E10.13.9.0"),sQuery(id+"F0.wireOp",EDGE,"E10.0.10.0"),sQuery(id+"F0.wireOp",EDGE,"E10.3.10.0"),sQuery(id+"F0.wireOp",EDGE,"E10.6.10.0"),sQuery(id+"F0.wireOp",EDGE,"E10.10.10.0"),sQuery(id+"F0.wireOp",EDGE,"E10.13.10.0"),sQuery(id+"F0.wireOp",EDGE,"E10.0.11.0"),sQuery(id+"F0.wireOp",EDGE,"E10.3.11.0"),sQuery(id+"F0.wireOp",EDGE,"E10.6.11.0"),sQuery(id+"F0.wireOp",EDGE,"E10.10.11.0"),sQuery(id+"F0.wireOp",EDGE,"E10.13.11.0"),sQuery(id+"F0.wireOp",EDGE,"E10.0.12.0"),sQuery(id+"F0.wireOp",EDGE,"E10.3.12.0"),sQuery(id+"F0.wireOp",EDGE,"E10.6.12.0"),sQuery(id+"F0.wireOp",EDGE,"E10.10.12.0"),sQuery(id+"F0.wireOp",EDGE,"E10.13.12.0"),sQuery(id+"F0.wireOp",EDGE,"E10.0.13.0"),sQuery(id+"F0.wireOp",EDGE,"E10.3.13.0"),sQuery(id+"F0.wireOp",EDGE,"E10.6.13.0"),sQuery(id+"F0.wireOp",EDGE,"E10.10.13.0"),sQuery(id+"F0.wireOp",EDGE,"E10.13.13.0"),sQuery(id+"F0.wireOp",EDGE,"E10.0.14.0"),sQuery(id+"F0.wireOp",EDGE,"E10.3.14.0"),sQuery(id+"F0.wireOp",EDGE,"E10.6.14.0"),sQuery(id+"F0.wireOp",EDGE,"E10.10.14.0"),sQuery(id+"F0.wireOp",EDGE,"E10.13.14.0"),sQuery(id+"F0.wireOp",EDGE,"E11"),sQuery(id+"F0.wireOp",EDGE,"E12"),sQuery(id+"F0.wireOp",EDGE,"E13"),sQuery(id+"F0.wireOp",EDGE,"E14"),sQuery(id+"F0.wireOp",EDGE,"E15")])]});
            var Q1;
            Q1=qCreatedBy(makeId("Right.planeOp"),FACE);
            transform(context, id + "F4", {"entities" : qUnion([Q0]), "transformType" : TransformType.TRANSLATION_DISTANCE, "transformDirection" : qUnion([Q1]), "distance" : 193 * mm, "oppositeDirection" : true, "makeCopy" : false});
        }
        {
            var Q0;
            Q0=makeQuery(id+"F1.opExtrude","SWEPT_BODY",BODY,{"disambiguationData":[OSD([sQuery(id+"F0.wireOp",EDGE,"E2"),sQuery(id+"F0.wireOp",EDGE,"E3"),sQuery(id+"F0.wireOp",EDGE,"E4"),sQuery(id+"F0.wireOp",EDGE,"E5"),sQuery(id+"F0.wireOp",EDGE,"E7"),sQuery(id+"F0.wireOp",EDGE,"E8.1.0.0"),sQuery(id+"F0.wireOp",EDGE,"E8.1.0.1"),sQuery(id+"F0.wireOp",EDGE,"E8.1.0.2"),sQuery(id+"F0.wireOp",EDGE,"E8.1.0.4"),sQuery(id+"F0.wireOp",EDGE,"E8.1.0.5"),sQuery(id+"F0.wireOp",EDGE,"E8.2.0.0"),sQuery(id+"F0.wireOp",EDGE,"E8.2.0.1"),sQuery(id+"F0.wireOp",EDGE,"E8.2.0.2"),sQuery(id+"F0.wireOp",EDGE,"E8.2.0.4"),sQuery(id+"F0.wireOp",EDGE,"E8.2.0.5"),sQuery(id+"F0.wireOp",EDGE,"E8.3.0.0"),sQuery(id+"F0.wireOp",EDGE,"E8.3.0.1"),sQuery(id+"F0.wireOp",EDGE,"E8.3.0.2"),sQuery(id+"F0.wireOp",EDGE,"E8.3.0.4"),sQuery(id+"F0.wireOp",EDGE,"E8.3.0.5"),sQuery(id+"F0.wireOp",EDGE,"E8.4.0.0"),sQuery(id+"F0.wireOp",EDGE,"E8.4.0.1"),sQuery(id+"F0.wireOp",EDGE,"E8.4.0.2"),sQuery(id+"F0.wireOp",EDGE,"E8.4.0.4"),sQuery(id+"F0.wireOp",EDGE,"E8.4.0.5"),sQuery(id+"F0.wireOp",EDGE,"E8.5.0.0"),sQuery(id+"F0.wireOp",EDGE,"E8.5.0.1"),sQuery(id+"F0.wireOp",EDGE,"E8.5.0.2"),sQuery(id+"F0.wireOp",EDGE,"E8.5.0.4"),sQuery(id+"F0.wireOp",EDGE,"E8.5.0.5"),sQuery(id+"F0.wireOp",EDGE,"E8.6.0.0"),sQuery(id+"F0.wireOp",EDGE,"E8.6.0.1"),sQuery(id+"F0.wireOp",EDGE,"E8.6.0.2"),sQuery(id+"F0.wireOp",EDGE,"E8.6.0.4"),sQuery(id+"F0.wireOp",EDGE,"E8.6.0.5"),sQuery(id+"F0.wireOp",EDGE,"E8.7.0.0"),sQuery(id+"F0.wireOp",EDGE,"E8.7.0.1"),sQuery(id+"F0.wireOp",EDGE,"E8.7.0.2"),sQuery(id+"F0.wireOp",EDGE,"E8.7.0.4"),sQuery(id+"F0.wireOp",EDGE,"E8.7.0.5"),sQuery(id+"F0.wireOp",EDGE,"E8.8.0.0"),sQuery(id+"F0.wireOp",EDGE,"E8.8.0.1"),sQuery(id+"F0.wireOp",EDGE,"E8.8.0.2"),sQuery(id+"F0.wireOp",EDGE,"E8.8.0.4"),sQuery(id+"F0.wireOp",EDGE,"E8.8.0.5"),sQuery(id+"F0.wireOp",EDGE,"E8.9.0.0"),sQuery(id+"F0.wireOp",EDGE,"E8.9.0.1"),sQuery(id+"F0.wireOp",EDGE,"E8.9.0.2"),sQuery(id+"F0.wireOp",EDGE,"E8.9.0.4"),sQuery(id+"F0.wireOp",EDGE,"E8.9.0.5"),sQuery(id+"F0.wireOp",EDGE,"E8.10.0.0"),sQuery(id+"F0.wireOp",EDGE,"E8.10.0.1"),sQuery(id+"F0.wireOp",EDGE,"E8.10.0.2"),sQuery(id+"F0.wireOp",EDGE,"E8.10.0.4"),sQuery(id+"F0.wireOp",EDGE,"E8.10.0.5"),sQuery(id+"F0.wireOp",EDGE,"E8.11.0.0"),sQuery(id+"F0.wireOp",EDGE,"E8.11.0.1"),sQuery(id+"F0.wireOp",EDGE,"E8.11.0.2"),sQuery(id+"F0.wireOp",EDGE,"E8.11.0.4"),sQuery(id+"F0.wireOp",EDGE,"E8.11.0.5"),sQuery(id+"F0.wireOp",EDGE,"E8.12.0.0"),sQuery(id+"F0.wireOp",EDGE,"E8.12.0.1"),sQuery(id+"F0.wireOp",EDGE,"E8.12.0.2"),sQuery(id+"F0.wireOp",EDGE,"E8.12.0.4"),sQuery(id+"F0.wireOp",EDGE,"E8.12.0.5"),sQuery(id+"F0.wireOp",EDGE,"E8.13.0.0"),sQuery(id+"F0.wireOp",EDGE,"E8.13.0.1"),sQuery(id+"F0.wireOp",EDGE,"E8.13.0.2"),sQuery(id+"F0.wireOp",EDGE,"E8.13.0.4"),sQuery(id+"F0.wireOp",EDGE,"E8.13.0.5"),sQuery(id+"F0.wireOp",EDGE,"E8.14.0.0"),sQuery(id+"F0.wireOp",EDGE,"E8.14.0.1"),sQuery(id+"F0.wireOp",EDGE,"E8.14.0.2"),sQuery(id+"F0.wireOp",EDGE,"E8.14.0.4"),sQuery(id+"F0.wireOp",EDGE,"E8.14.0.5"),sQuery(id+"F0.wireOp",EDGE,"E9.1.0.0"),sQuery(id+"F0.wireOp",EDGE,"E9.1.0.1"),sQuery(id+"F0.wireOp",EDGE,"E9.1.0.2"),sQuery(id+"F0.wireOp",EDGE,"E9.1.0.4"),sQuery(id+"F0.wireOp",EDGE,"E9.1.0.5"),sQuery(id+"F0.wireOp",EDGE,"E9.2.0.0"),sQuery(id+"F0.wireOp",EDGE,"E9.2.0.1"),sQuery(id+"F0.wireOp",EDGE,"E9.2.0.2"),sQuery(id+"F0.wireOp",EDGE,"E9.2.0.4"),sQuery(id+"F0.wireOp",EDGE,"E9.2.0.5"),sQuery(id+"F0.wireOp",EDGE,"E10.0.3.0"),sQuery(id+"F0.wireOp",EDGE,"E10.3.3.0"),sQuery(id+"F0.wireOp",EDGE,"E10.6.3.0"),sQuery(id+"F0.wireOp",EDGE,"E10.10.3.0"),sQuery(id+"F0.wireOp",EDGE,"E10.13.3.0"),sQuery(id+"F0.wireOp",EDGE,"E10.0.4.0"),sQuery(id+"F0.wireOp",EDGE,"E10.3.4.0"),sQuery(id+"F0.wireOp",EDGE,"E10.6.4.0"),sQuery(id+"F0.wireOp",EDGE,"E10.10.4.0"),sQuery(id+"F0.wireOp",EDGE,"E10.13.4.0"),sQuery(id+"F0.wireOp",EDGE,"E10.0.5.0"),sQuery(id+"F0.wireOp",EDGE,"E10.3.5.0"),sQuery(id+"F0.wireOp",EDGE,"E10.6.5.0"),sQuery(id+"F0.wireOp",EDGE,"E10.10.5.0"),sQuery(id+"F0.wireOp",EDGE,"E10.13.5.0"),sQuery(id+"F0.wireOp",EDGE,"E10.0.6.0"),sQuery(id+"F0.wireOp",EDGE,"E10.3.6.0"),sQuery(id+"F0.wireOp",EDGE,"E10.6.6.0"),sQuery(id+"F0.wireOp",EDGE,"E10.10.6.0"),sQuery(id+"F0.wireOp",EDGE,"E10.13.6.0"),sQuery(id+"F0.wireOp",EDGE,"E10.0.7.0"),sQuery(id+"F0.wireOp",EDGE,"E10.3.7.0"),sQuery(id+"F0.wireOp",EDGE,"E10.6.7.0"),sQuery(id+"F0.wireOp",EDGE,"E10.10.7.0"),sQuery(id+"F0.wireOp",EDGE,"E10.13.7.0"),sQuery(id+"F0.wireOp",EDGE,"E10.0.8.0"),sQuery(id+"F0.wireOp",EDGE,"E10.3.8.0"),sQuery(id+"F0.wireOp",EDGE,"E10.6.8.0"),sQuery(id+"F0.wireOp",EDGE,"E10.10.8.0"),sQuery(id+"F0.wireOp",EDGE,"E10.13.8.0"),sQuery(id+"F0.wireOp",EDGE,"E10.0.9.0"),sQuery(id+"F0.wireOp",EDGE,"E10.3.9.0"),sQuery(id+"F0.wireOp",EDGE,"E10.6.9.0"),sQuery(id+"F0.wireOp",EDGE,"E10.10.9.0"),sQuery(id+"F0.wireOp",EDGE,"E10.13.9.0"),sQuery(id+"F0.wireOp",EDGE,"E10.0.10.0"),sQuery(id+"F0.wireOp",EDGE,"E10.3.10.0"),sQuery(id+"F0.wireOp",EDGE,"E10.6.10.0"),sQuery(id+"F0.wireOp",EDGE,"E10.10.10.0"),sQuery(id+"F0.wireOp",EDGE,"E10.13.10.0"),sQuery(id+"F0.wireOp",EDGE,"E10.0.11.0"),sQuery(id+"F0.wireOp",EDGE,"E10.3.11.0"),sQuery(id+"F0.wireOp",EDGE,"E10.6.11.0"),sQuery(id+"F0.wireOp",EDGE,"E10.10.11.0"),sQuery(id+"F0.wireOp",EDGE,"E10.13.11.0"),sQuery(id+"F0.wireOp",EDGE,"E10.0.12.0"),sQuery(id+"F0.wireOp",EDGE,"E10.3.12.0"),sQuery(id+"F0.wireOp",EDGE,"E10.6.12.0"),sQuery(id+"F0.wireOp",EDGE,"E10.10.12.0"),sQuery(id+"F0.wireOp",EDGE,"E10.13.12.0"),sQuery(id+"F0.wireOp",EDGE,"E10.0.13.0"),sQuery(id+"F0.wireOp",EDGE,"E10.3.13.0"),sQuery(id+"F0.wireOp",EDGE,"E10.6.13.0"),sQuery(id+"F0.wireOp",EDGE,"E10.10.13.0"),sQuery(id+"F0.wireOp",EDGE,"E10.13.13.0"),sQuery(id+"F0.wireOp",EDGE,"E10.0.14.0"),sQuery(id+"F0.wireOp",EDGE,"E10.3.14.0"),sQuery(id+"F0.wireOp",EDGE,"E10.6.14.0"),sQuery(id+"F0.wireOp",EDGE,"E10.10.14.0"),sQuery(id+"F0.wireOp",EDGE,"E10.13.14.0"),sQuery(id+"F0.wireOp",EDGE,"E11"),sQuery(id+"F0.wireOp",EDGE,"E12"),sQuery(id+"F0.wireOp",EDGE,"E13"),sQuery(id+"F0.wireOp",EDGE,"E14"),sQuery(id+"F0.wireOp",EDGE,"E15")])]});
            var Q1;
            Q1=qCreatedBy(makeId("Front.planeOp"),FACE);
            transform(context, id + "F5", {"entities" : qUnion([Q0]), "transformType" : TransformType.TRANSLATION_DISTANCE, "transformDirection" : qUnion([Q1]), "distance" : 5 * mm, "makeCopy" : false});
        }
        {
            var Q0;
            Q0=makeQuery(id+"F1.opExtrude","SWEPT_BODY",BODY,{"disambiguationData":[OSD([sQuery(id+"F0.wireOp",EDGE,"E2"),sQuery(id+"F0.wireOp",EDGE,"E3"),sQuery(id+"F0.wireOp",EDGE,"E4"),sQuery(id+"F0.wireOp",EDGE,"E5"),sQuery(id+"F0.wireOp",EDGE,"E7"),sQuery(id+"F0.wireOp",EDGE,"E8.1.0.0"),sQuery(id+"F0.wireOp",EDGE,"E8.1.0.1"),sQuery(id+"F0.wireOp",EDGE,"E8.1.0.2"),sQuery(id+"F0.wireOp",EDGE,"E8.1.0.4"),sQuery(id+"F0.wireOp",EDGE,"E8.1.0.5"),sQuery(id+"F0.wireOp",EDGE,"E8.2.0.0"),sQuery(id+"F0.wireOp",EDGE,"E8.2.0.1"),sQuery(id+"F0.wireOp",EDGE,"E8.2.0.2"),sQuery(id+"F0.wireOp",EDGE,"E8.2.0.4"),sQuery(id+"F0.wireOp",EDGE,"E8.2.0.5"),sQuery(id+"F0.wireOp",EDGE,"E8.3.0.0"),sQuery(id+"F0.wireOp",EDGE,"E8.3.0.1"),sQuery(id+"F0.wireOp",EDGE,"E8.3.0.2"),sQuery(id+"F0.wireOp",EDGE,"E8.3.0.4"),sQuery(id+"F0.wireOp",EDGE,"E8.3.0.5"),sQuery(id+"F0.wireOp",EDGE,"E8.4.0.0"),sQuery(id+"F0.wireOp",EDGE,"E8.4.0.1"),sQuery(id+"F0.wireOp",EDGE,"E8.4.0.2"),sQuery(id+"F0.wireOp",EDGE,"E8.4.0.4"),sQuery(id+"F0.wireOp",EDGE,"E8.4.0.5"),sQuery(id+"F0.wireOp",EDGE,"E8.5.0.0"),sQuery(id+"F0.wireOp",EDGE,"E8.5.0.1"),sQuery(id+"F0.wireOp",EDGE,"E8.5.0.2"),sQuery(id+"F0.wireOp",EDGE,"E8.5.0.4"),sQuery(id+"F0.wireOp",EDGE,"E8.5.0.5"),sQuery(id+"F0.wireOp",EDGE,"E8.6.0.0"),sQuery(id+"F0.wireOp",EDGE,"E8.6.0.1"),sQuery(id+"F0.wireOp",EDGE,"E8.6.0.2"),sQuery(id+"F0.wireOp",EDGE,"E8.6.0.4"),sQuery(id+"F0.wireOp",EDGE,"E8.6.0.5"),sQuery(id+"F0.wireOp",EDGE,"E8.7.0.0"),sQuery(id+"F0.wireOp",EDGE,"E8.7.0.1"),sQuery(id+"F0.wireOp",EDGE,"E8.7.0.2"),sQuery(id+"F0.wireOp",EDGE,"E8.7.0.4"),sQuery(id+"F0.wireOp",EDGE,"E8.7.0.5"),sQuery(id+"F0.wireOp",EDGE,"E8.8.0.0"),sQuery(id+"F0.wireOp",EDGE,"E8.8.0.1"),sQuery(id+"F0.wireOp",EDGE,"E8.8.0.2"),sQuery(id+"F0.wireOp",EDGE,"E8.8.0.4"),sQuery(id+"F0.wireOp",EDGE,"E8.8.0.5"),sQuery(id+"F0.wireOp",EDGE,"E8.9.0.0"),sQuery(id+"F0.wireOp",EDGE,"E8.9.0.1"),sQuery(id+"F0.wireOp",EDGE,"E8.9.0.2"),sQuery(id+"F0.wireOp",EDGE,"E8.9.0.4"),sQuery(id+"F0.wireOp",EDGE,"E8.9.0.5"),sQuery(id+"F0.wireOp",EDGE,"E8.10.0.0"),sQuery(id+"F0.wireOp",EDGE,"E8.10.0.1"),sQuery(id+"F0.wireOp",EDGE,"E8.10.0.2"),sQuery(id+"F0.wireOp",EDGE,"E8.10.0.4"),sQuery(id+"F0.wireOp",EDGE,"E8.10.0.5"),sQuery(id+"F0.wireOp",EDGE,"E8.11.0.0"),sQuery(id+"F0.wireOp",EDGE,"E8.11.0.1"),sQuery(id+"F0.wireOp",EDGE,"E8.11.0.2"),sQuery(id+"F0.wireOp",EDGE,"E8.11.0.4"),sQuery(id+"F0.wireOp",EDGE,"E8.11.0.5"),sQuery(id+"F0.wireOp",EDGE,"E8.12.0.0"),sQuery(id+"F0.wireOp",EDGE,"E8.12.0.1"),sQuery(id+"F0.wireOp",EDGE,"E8.12.0.2"),sQuery(id+"F0.wireOp",EDGE,"E8.12.0.4"),sQuery(id+"F0.wireOp",EDGE,"E8.12.0.5"),sQuery(id+"F0.wireOp",EDGE,"E8.13.0.0"),sQuery(id+"F0.wireOp",EDGE,"E8.13.0.1"),sQuery(id+"F0.wireOp",EDGE,"E8.13.0.2"),sQuery(id+"F0.wireOp",EDGE,"E8.13.0.4"),sQuery(id+"F0.wireOp",EDGE,"E8.13.0.5"),sQuery(id+"F0.wireOp",EDGE,"E8.14.0.0"),sQuery(id+"F0.wireOp",EDGE,"E8.14.0.1"),sQuery(id+"F0.wireOp",EDGE,"E8.14.0.2"),sQuery(id+"F0.wireOp",EDGE,"E8.14.0.4"),sQuery(id+"F0.wireOp",EDGE,"E8.14.0.5"),sQuery(id+"F0.wireOp",EDGE,"E9.1.0.0"),sQuery(id+"F0.wireOp",EDGE,"E9.1.0.1"),sQuery(id+"F0.wireOp",EDGE,"E9.1.0.2"),sQuery(id+"F0.wireOp",EDGE,"E9.1.0.4"),sQuery(id+"F0.wireOp",EDGE,"E9.1.0.5"),sQuery(id+"F0.wireOp",EDGE,"E9.2.0.0"),sQuery(id+"F0.wireOp",EDGE,"E9.2.0.1"),sQuery(id+"F0.wireOp",EDGE,"E9.2.0.2"),sQuery(id+"F0.wireOp",EDGE,"E9.2.0.4"),sQuery(id+"F0.wireOp",EDGE,"E9.2.0.5"),sQuery(id+"F0.wireOp",EDGE,"E10.0.3.0"),sQuery(id+"F0.wireOp",EDGE,"E10.3.3.0"),sQuery(id+"F0.wireOp",EDGE,"E10.6.3.0"),sQuery(id+"F0.wireOp",EDGE,"E10.10.3.0"),sQuery(id+"F0.wireOp",EDGE,"E10.13.3.0"),sQuery(id+"F0.wireOp",EDGE,"E10.0.4.0"),sQuery(id+"F0.wireOp",EDGE,"E10.3.4.0"),sQuery(id+"F0.wireOp",EDGE,"E10.6.4.0"),sQuery(id+"F0.wireOp",EDGE,"E10.10.4.0"),sQuery(id+"F0.wireOp",EDGE,"E10.13.4.0"),sQuery(id+"F0.wireOp",EDGE,"E10.0.5.0"),sQuery(id+"F0.wireOp",EDGE,"E10.3.5.0"),sQuery(id+"F0.wireOp",EDGE,"E10.6.5.0"),sQuery(id+"F0.wireOp",EDGE,"E10.10.5.0"),sQuery(id+"F0.wireOp",EDGE,"E10.13.5.0"),sQuery(id+"F0.wireOp",EDGE,"E10.0.6.0"),sQuery(id+"F0.wireOp",EDGE,"E10.3.6.0"),sQuery(id+"F0.wireOp",EDGE,"E10.6.6.0"),sQuery(id+"F0.wireOp",EDGE,"E10.10.6.0"),sQuery(id+"F0.wireOp",EDGE,"E10.13.6.0"),sQuery(id+"F0.wireOp",EDGE,"E10.0.7.0"),sQuery(id+"F0.wireOp",EDGE,"E10.3.7.0"),sQuery(id+"F0.wireOp",EDGE,"E10.6.7.0"),sQuery(id+"F0.wireOp",EDGE,"E10.10.7.0"),sQuery(id+"F0.wireOp",EDGE,"E10.13.7.0"),sQuery(id+"F0.wireOp",EDGE,"E10.0.8.0"),sQuery(id+"F0.wireOp",EDGE,"E10.3.8.0"),sQuery(id+"F0.wireOp",EDGE,"E10.6.8.0"),sQuery(id+"F0.wireOp",EDGE,"E10.10.8.0"),sQuery(id+"F0.wireOp",EDGE,"E10.13.8.0"),sQuery(id+"F0.wireOp",EDGE,"E10.0.9.0"),sQuery(id+"F0.wireOp",EDGE,"E10.3.9.0"),sQuery(id+"F0.wireOp",EDGE,"E10.6.9.0"),sQuery(id+"F0.wireOp",EDGE,"E10.10.9.0"),sQuery(id+"F0.wireOp",EDGE,"E10.13.9.0"),sQuery(id+"F0.wireOp",EDGE,"E10.0.10.0"),sQuery(id+"F0.wireOp",EDGE,"E10.3.10.0"),sQuery(id+"F0.wireOp",EDGE,"E10.6.10.0"),sQuery(id+"F0.wireOp",EDGE,"E10.10.10.0"),sQuery(id+"F0.wireOp",EDGE,"E10.13.10.0"),sQuery(id+"F0.wireOp",EDGE,"E10.0.11.0"),sQuery(id+"F0.wireOp",EDGE,"E10.3.11.0"),sQuery(id+"F0.wireOp",EDGE,"E10.6.11.0"),sQuery(id+"F0.wireOp",EDGE,"E10.10.11.0"),sQuery(id+"F0.wireOp",EDGE,"E10.13.11.0"),sQuery(id+"F0.wireOp",EDGE,"E10.0.12.0"),sQuery(id+"F0.wireOp",EDGE,"E10.3.12.0"),sQuery(id+"F0.wireOp",EDGE,"E10.6.12.0"),sQuery(id+"F0.wireOp",EDGE,"E10.10.12.0"),sQuery(id+"F0.wireOp",EDGE,"E10.13.12.0"),sQuery(id+"F0.wireOp",EDGE,"E10.0.13.0"),sQuery(id+"F0.wireOp",EDGE,"E10.3.13.0"),sQuery(id+"F0.wireOp",EDGE,"E10.6.13.0"),sQuery(id+"F0.wireOp",EDGE,"E10.10.13.0"),sQuery(id+"F0.wireOp",EDGE,"E10.13.13.0"),sQuery(id+"F0.wireOp",EDGE,"E10.0.14.0"),sQuery(id+"F0.wireOp",EDGE,"E10.3.14.0"),sQuery(id+"F0.wireOp",EDGE,"E10.6.14.0"),sQuery(id+"F0.wireOp",EDGE,"E10.10.14.0"),sQuery(id+"F0.wireOp",EDGE,"E10.13.14.0"),sQuery(id+"F0.wireOp",EDGE,"E11"),sQuery(id+"F0.wireOp",EDGE,"E12"),sQuery(id+"F0.wireOp",EDGE,"E13"),sQuery(id+"F0.wireOp",EDGE,"E14"),sQuery(id+"F0.wireOp",EDGE,"E15")])]});
            var Q1;
            Q1=qCreatedBy(makeId("Right.planeOp"),FACE);
            mirror(context, id + "F6", {"entities" : qUnion([Q0]), "mirrorPlane" : qUnion([Q1])});
        }
        {
            var Q0;
            Q0=makeQuery(id+"F1.opExtrude","SWEPT_FACE",FACE,{"disambiguationData":[OSD([sQuery(id+"F0.wireOp",EDGE,"E12")])]});
            var sketch = newSketch(context, id + "F7", { "sketchPlane" : qUnion([Q0])});
            skLineSegment(sketch, "E21.0", {"start": v(-242, 0) * mm, "end": v(-193, 0) * mm});
            skLineSegment(sketch, "E21.1", {"start": v(-193, 75) * mm, "end": v(-193, 0) * mm});
            skLineSegment(sketch, "E22", {"start": v(0, 0) * mm, "end": v(0, 130.75) * mm, "construction": true});
            skLineSegment(sketch, "E23", {"start": v(-193, 75) * mm, "end": v(0, 75) * mm});
            skLineSegment(sketch, "E24", {"start": v(-197, -50) * mm, "end": v(0, -50) * mm});
            skLineSegment(sketch, "E25", {"start": v(-242, 0) * mm, "end": v(-242, -8) * mm});
            skLineSegment(sketch, "E26", {"start": v(-240.4, -11.67) * mm, "end": v(-200.4, -48.67) * mm, "construction": true});
            skPoint(sketch, "E27.visualSharp", {"position": v(-242, -10.19) * mm});
            skArc(sketch, "E27.filletArc", {"start": v(-242, -8) * mm, "mid": v(-241.58, -10) * mm, "end": v(-240.4, -11.67) * mm, "construction": true});
            skPoint(sketch, "E28.visualSharp", {"position": v(-198.96, -50) * mm});
            skArc(sketch, "E28.filletArc", {"start": v(-200.4, -48.67) * mm, "mid": v(-198.82, -49.66) * mm, "end": v(-197, -50) * mm, "construction": true});
            skArc(sketch, "E29.MirrorCS", {"start": v(242, -8) * mm, "mid": v(241.58, -10) * mm, "end": v(240.4, -11.67) * mm, "construction": true});
            skArc(sketch, "E30.MirrorCS", {"start": v(200.4, -48.67) * mm, "mid": v(198.82, -49.66) * mm, "end": v(197, -50) * mm, "construction": true});
            skLineSegment(sketch, "E31.MirrorCS", {"start": v(242, 0) * mm, "end": v(242, -8) * mm, "construction": true});
            skPoint(sketch, "E32.MirrorP", {"position": v(242, -10.19) * mm});
            skLineSegment(sketch, "E33.MirrorCS", {"start": v(240.4, -11.67) * mm, "end": v(200.4, -48.67) * mm, "construction": true});
            skLineSegment(sketch, "E34.MirrorCS", {"start": v(193, 75) * mm, "end": v(0, 75) * mm});
            skLineSegment(sketch, "E35.MirrorCS", {"start": v(197, -50) * mm, "end": v(0, -50) * mm});
            skLineSegment(sketch, "E36.MirrorCS", {"start": v(193, 75) * mm, "end": v(193, 0) * mm});
            skPoint(sketch, "E37.MirrorP", {"position": v(198.96, -50) * mm});
            skLineSegment(sketch, "E38", {"start": v(-242, -8) * mm, "end": v(-242, -45) * mm});
            skLineSegment(sketch, "E39", {"start": v(-237, -50) * mm, "end": v(-197, -50) * mm});
            skLineSegment(sketch, "E40", {"start": v(242, 0) * mm, "end": v(242, -45) * mm});
            skPoint(sketch, "E40.endSnap0", {"position": v(242, -4) * mm});
            skLineSegment(sketch, "E41", {"start": v(237, -50) * mm, "end": v(197, -50) * mm});
            skLineSegment(sketch, "E42", {"start": v(193, 0) * mm, "end": v(242, 0) * mm});
            skPoint(sketch, "E43.visualSharp", {"position": v(-242, -50) * mm});
            skArc(sketch, "E43.filletArc", {"start": v(-242, -45) * mm, "mid": v(-240.54, -48.54) * mm, "end": v(-237, -50) * mm});
            skPoint(sketch, "E44.visualSharp", {"position": v(242, -50) * mm});
            skArc(sketch, "E44.filletArc", {"start": v(237, -50) * mm, "mid": v(240.54, -48.54) * mm, "end": v(242, -45) * mm});
            skSolve(sketch);
        }
        {
            var Q0;
            Q0=makeQuery(id+"F7.imprint","IMPRINT",FACE,{"disambiguationData":[TD([[makeQuery(id+"F7.imprint","IMPRINT",EDGE,{"derivedFrom":sQuery(id+"F7.wireOp",EDGE,"E21.0")}),-1.0]])]});
            extrude(context, id + "F8", {"entities" : qUnion([Q0]), "oppositeDirection" : true, "depth" : 4 * mm});
        }
        {
            var Q0;
            Q0=makeQuery(id+"F8.opExtrude","SWEPT_BODY",BODY,{"disambiguationData":[OSD([sQuery(id+"F7.wireOp",EDGE,"E21.0"),sQuery(id+"F7.wireOp",EDGE,"E21.1"),sQuery(id+"F7.wireOp",EDGE,"E23"),sQuery(id+"F7.wireOp",EDGE,"E24"),sQuery(id+"F7.wireOp",EDGE,"E25"),sQuery(id+"F7.wireOp",EDGE,"E26"),sQuery(id+"F7.wireOp",EDGE,"E27.filletArc"),sQuery(id+"F7.wireOp",EDGE,"E28.filletArc"),sQuery(id+"F7.wireOp",EDGE,"E29.MirrorCS"),sQuery(id+"F7.wireOp",EDGE,"E30.MirrorCS"),sQuery(id+"F7.wireOp",EDGE,"E31.MirrorCS"),sQuery(id+"F7.wireOp",EDGE,"E33.MirrorCS"),sQuery(id+"F7.wireOp",EDGE,"E34.MirrorCS"),sQuery(id+"F7.wireOp",EDGE,"E35.MirrorCS"),sQuery(id+"F7.wireOp",EDGE,"E36.MirrorCS"),sQuery(id+"F7.wireOp",EDGE,"4e9f4d0c-7754-498c-804e-4cfdb606c8ca8.MirrorCS")])]});
            var Q1;
            Q1=qCreatedBy(makeId("Front.planeOp"),FACE);
            mirror(context, id + "F9", {"entities" : qUnion([Q0]), "mirrorPlane" : qUnion([Q1])});
        }
        {
            var Q0;
            Q0=makeQuery(id+"F9.opPattern","COPY",FACE,{"derivedFrom":makeQuery(id+"F8.opExtrude","SWEPT_FACE",FACE,{"disambiguationData":[OSD([sQuery(id+"F7.wireOp",EDGE,"E23"),sQuery(id+"F7.wireOp",EDGE,"E34.MirrorCS")])]}),"instanceName":"1"});
            var sketch = newSketch(context, id + "F10", { "sketchPlane" : qUnion([Q0])});
            skLineSegment(sketch, "E45.0", {"start": v(193, 150) * mm, "end": v(-193, 150) * mm});
            skLineSegment(sketch, "E45.1", {"start": v(-193, -150) * mm, "end": v(-193, 150) * mm});
            skLineSegment(sketch, "E45.2", {"start": v(193, -150) * mm, "end": v(-193, -150) * mm});
            skLineSegment(sketch, "E45.3", {"start": v(193, -150) * mm, "end": v(193, 150) * mm});
            skSolve(sketch);
        }
        {
            var Q0;
            Q0 = qSketchRegion(id + "F10", true);
            extrude(context, id + "F11", {"entities" : qUnion([Q0]), "depth" : 4 * mm});
        }
        {
            var Q0;
            Q0=makeQuery(id+"F8.opExtrude","SWEPT_FACE",FACE,{"disambiguationData":[OSD([sQuery(id+"F7.wireOp",EDGE,"E24"),sQuery(id+"F7.wireOp",EDGE,"E35.MirrorCS"),sQuery(id+"F7.wireOp",EDGE,"E39"),sQuery(id+"F7.wireOp",EDGE,"E41")])]});
            var sketch = newSketch(context, id + "F12", { "sketchPlane" : qUnion([Q0])});
            skLineSegment(sketch, "E46.0", {"start": v(193, -146) * mm, "end": v(-193, -146) * mm});
            skLineSegment(sketch, "E46.1", {"start": v(193, 146) * mm, "end": v(-193, 146) * mm});
            skLineSegment(sketch, "E47", {"start": v(193, -146) * mm, "end": v(193, 146) * mm});
            skLineSegment(sketch, "E48", {"start": v(-193, -146) * mm, "end": v(-193, 146) * mm});
            skLineSegment(sketch, "E49", {"start": v(0, 0) * mm, "end": v(0, -82.25) * mm, "construction": true});
            skLineSegment(sketch, "E50", {"start": v(0, 0) * mm, "end": v(80, 0) * mm, "construction": true});
            skCircle(sketch, "E51", {"center": v(-168, -121) * mm, "radius": 2.25 * mm});
            skCircle(sketch, "E52.MirrorC", {"center": v(168, -121) * mm, "radius": 2.25 * mm});
            skLineSegment(sketch, "E53.MirrorCS", {"start": v(0, 0) * mm, "end": v(-80, 0) * mm, "construction": true});
            skCircle(sketch, "E54.MirrorC", {"center": v(-168, 121) * mm, "radius": 2.25 * mm});
            skCircle(sketch, "E55.MirrorC", {"center": v(168, 121) * mm, "radius": 2.25 * mm});
            skCircle(sketch, "E56", {"center": v(-80, 0) * mm, "radius": 3.25 * mm});
            skCircle(sketch, "E57", {"center": v(80, 0) * mm, "radius": 3.25 * mm});
            skCircle(sketch, "E58", {"center": v(0, -82.25) * mm, "radius": 2.25 * mm});
            skSolve(sketch);
        }
        {
            var Q0;
            Q0 = qSketchRegion(id + "F12", true);
            extrude(context, id + "F13", {"entities" : qUnion([Q0]), "oppositeDirection" : true, "depth" : 4 * mm});
        }
        {
            var Q0;
            Q0=makeQuery(id+"F1.opExtrude","SWEPT_FACE",FACE,{"disambiguationData":[OSD([sQuery(id+"F0.wireOp",EDGE,"E13")])]});
            var sketch = newSketch(context, id + "F14", { "sketchPlane" : qUnion([Q0])});
            skLineSegment(sketch, "E59.bottom", {"start": v(146, -50) * mm, "end": v(-146, -50) * mm});
            skLineSegment(sketch, "E59.top", {"start": v(146, 0) * mm, "end": v(-146, 0) * mm});
            skLineSegment(sketch, "E59.left", {"start": v(146, -50) * mm, "end": v(146, 0) * mm});
            skLineSegment(sketch, "E59.right", {"start": v(-146, -50) * mm, "end": v(-146, 0) * mm});
            skSolve(sketch);
        }
        {
            var Q0;
            Q0 = qSketchRegion(id + "F14", true);
            extrude(context, id + "F15", {"entities" : qUnion([Q0]), "oppositeDirection" : true, "depth" : 4 * mm});
        }
        {
            var Q0;
            Q0=makeQuery(id+"F11.opExtrude","CAP_FACE",FACE,{"disambiguationData":[OSD([sQuery(id+"F10.wireOp",EDGE,"E45.0"),sQuery(id+"F10.wireOp",EDGE,"E45.1"),sQuery(id+"F10.wireOp",EDGE,"E45.2"),sQuery(id+"F10.wireOp",EDGE,"E45.3")])],"isStart":true});
            var sketch = newSketch(context, id + "F16", { "sketchPlane" : qUnion([Q0])});
            skLineSegment(sketch, "E60", {"start": v(-177, 146) * mm, "end": v(-193, 146) * mm});
            skLineSegment(sketch, "E61", {"start": v(-193, 146) * mm, "end": v(-193, 130) * mm});
            skLineSegment(sketch, "E62", {"start": v(-193, 130) * mm, "end": v(-190, 130) * mm});
            skLineSegment(sketch, "E63", {"start": v(-190, 130) * mm, "end": v(-190, 143) * mm});
            skLineSegment(sketch, "E64", {"start": v(-190, 143) * mm, "end": v(-177, 143) * mm});
            skLineSegment(sketch, "E65", {"start": v(-177, 143) * mm, "end": v(-177, 146) * mm});
            skSolve(sketch);
        }
        {
            var Q0;
            Q0 = qSketchRegion(id + "F16", true);
            var Q1;
            Q1=makeQuery(id+"F13.opExtrude","CAP_FACE",FACE,{"disambiguationData":[OSD([sQuery(id+"F12.wireOp",EDGE,"E46.0"),sQuery(id+"F12.wireOp",EDGE,"E46.1"),sQuery(id+"F12.wireOp",EDGE,"E47"),sQuery(id+"F12.wireOp",EDGE,"E48")])],"isStart":false});
            extrude(context, id + "F17", {"entities" : qUnion([Q0]), "endBound" : BoundingType.UP_TO_SURFACE, "endBoundEntityFace" : qUnion([Q1]), "depth" : 25 * mm});
        }
        {
            var Q0;
            Q0=makeQuery(id+"F17.opExtrude","SWEPT_BODY",BODY,{"disambiguationData":[OSD([sQuery(id+"F16.wireOp",EDGE,"E60"),sQuery(id+"F16.wireOp",EDGE,"E61"),sQuery(id+"F16.wireOp",EDGE,"E62"),sQuery(id+"F16.wireOp",EDGE,"E63"),sQuery(id+"F16.wireOp",EDGE,"E64"),sQuery(id+"F16.wireOp",EDGE,"E65")])]});
            var Q1;
            Q1=qCreatedBy(makeId("Front.planeOp"),FACE);
            mirror(context, id + "F18", {"entities" : qUnion([Q0]), "mirrorPlane" : qUnion([Q1])});
        }
        {
            var Q0;
            Q0=makeQuery(id+"F18.opPattern","COPY",BODY,{"derivedFrom":makeQuery(id+"F17.opExtrude","SWEPT_BODY",BODY,{"disambiguationData":[OSD([sQuery(id+"F16.wireOp",EDGE,"E60"),sQuery(id+"F16.wireOp",EDGE,"E61"),sQuery(id+"F16.wireOp",EDGE,"E62"),sQuery(id+"F16.wireOp",EDGE,"E63"),sQuery(id+"F16.wireOp",EDGE,"E64"),sQuery(id+"F16.wireOp",EDGE,"E65")])]}),"instanceName":"1"});
            var Q1;
            Q1=makeQuery(id+"F17.opExtrude","SWEPT_BODY",BODY,{"disambiguationData":[OSD([sQuery(id+"F16.wireOp",EDGE,"E60"),sQuery(id+"F16.wireOp",EDGE,"E61"),sQuery(id+"F16.wireOp",EDGE,"E62"),sQuery(id+"F16.wireOp",EDGE,"E63"),sQuery(id+"F16.wireOp",EDGE,"E64"),sQuery(id+"F16.wireOp",EDGE,"E65")])]});
            var Q2;
            Q2=qCreatedBy(makeId("Right.planeOp"),FACE);
            mirror(context, id + "F19", {"entities" : qUnion([Q0, Q1]), "mirrorPlane" : qUnion([Q2])});
        }
        {
            var Q0;
            Q0=makeQuery(id+"F11.opExtrude","CAP_FACE",FACE,{"disambiguationData":[OSD([sQuery(id+"F10.wireOp",EDGE,"E45.0"),sQuery(id+"F10.wireOp",EDGE,"E45.1"),sQuery(id+"F10.wireOp",EDGE,"E45.2"),sQuery(id+"F10.wireOp",EDGE,"E45.3")])],"isStart":false});
            var sketch = newSketch(context, id + "F20", { "sketchPlane" : qUnion([Q0])});
            skLineSegment(sketch, "E66.bottom", {"start": v(-50, 50) * mm, "end": v(50, 50) * mm, "construction": true});
            skLineSegment(sketch, "E66.top", {"start": v(-50, -50) * mm, "end": v(50, -50) * mm, "construction": true});
            skLineSegment(sketch, "E66.left", {"start": v(-50, 50) * mm, "end": v(-50, -50) * mm, "construction": true});
            skLineSegment(sketch, "E66.right", {"start": v(50, 50) * mm, "end": v(50, -50) * mm, "construction": true});
            skLineSegment(sketch, "E67", {"start": v(0, 0) * mm, "end": v(0, 50) * mm, "construction": true});
            skLineSegment(sketch, "E68", {"start": v(0, 0) * mm, "end": v(50, 0) * mm, "construction": true});
            skCircle(sketch, "E69", {"center": v(-50, 50) * mm, "radius": 12.5 * mm});
            skCircle(sketch, "E70", {"center": v(50, 50) * mm, "radius": 12.5 * mm});
            skCircle(sketch, "E71", {"center": v(50, -50) * mm, "radius": 12.5 * mm});
            skCircle(sketch, "E72", {"center": v(-50, -50) * mm, "radius": 12.5 * mm});
            skSolve(sketch);
        }
        {
            var Q0;
            Q0 = qSketchRegion(id + "F20", true);
            extrude(context, id + "F21", {"entities" : qUnion([Q0]), "operationType" : NewBodyOperationType.REMOVE, "endBound" : BoundingType.UP_TO_NEXT, "oppositeDirection" : true, "depth" : 25 * mm});
        }
        {
            var Q0;
            Q0=makeQuery(id+"F17.opExtrude","SWEPT_FACE",FACE,{"disambiguationData":[OSD([sQuery(id+"F16.wireOp",EDGE,"E65")])]});
            var sketch = newSketch(context, id + "F22", { "sketchPlane" : qUnion([Q0])});
            skPoint(sketch, "E73.orphan", {"position": v(-150, 75) * mm});
            skPoint(sketch, "E74.orphan", {"position": v(150, 75) * mm});
            skPoint(sketch, "E75.orphan", {"position": v(-130, -46) * mm});
            skLineSegment(sketch, "E76.0", {"start": v(-146, 59) * mm, "end": v(-146, 75) * mm});
            skLineSegment(sketch, "E77", {"start": v(-146, 75) * mm, "end": v(-130, 75) * mm});
            skLineSegment(sketch, "E78", {"start": v(-130, 75) * mm, "end": v(-130, 72) * mm});
            skLineSegment(sketch, "E79", {"start": v(-130, 72) * mm, "end": v(-143, 72) * mm});
            skLineSegment(sketch, "E80", {"start": v(-143, 72) * mm, "end": v(-143, 59) * mm});
            skLineSegment(sketch, "E81", {"start": v(-143, 59) * mm, "end": v(-146, 59) * mm});
            skPoint(sketch, "E82.orphan", {"position": v(-146, -46) * mm});
            skSolve(sketch);
        }
        {
            var Q0;
            Q0 = qSketchRegion(id + "F22", true);
            var Q1;
            Q1=makeQuery(id+"F19.opPattern","COPY",FACE,{"derivedFrom":makeQuery(id+"F17.opExtrude","SWEPT_FACE",FACE,{"disambiguationData":[OSD([sQuery(id+"F16.wireOp",EDGE,"E65")])]}),"instanceName":"1"});
            extrude(context, id + "F23", {"entities" : qUnion([Q0]), "endBound" : BoundingType.UP_TO_SURFACE, "endBoundEntityFace" : qUnion([Q1]), "depth" : 25 * mm});
        }
        {
            var Q0;
            Q0=makeQuery(id+"F23.opExtrude","SWEPT_BODY",BODY,{"disambiguationData":[OSD([sQuery(id+"F22.wireOp",EDGE,"E76.0"),sQuery(id+"F22.wireOp",EDGE,"E77"),sQuery(id+"F22.wireOp",EDGE,"E78"),sQuery(id+"F22.wireOp",EDGE,"E79"),sQuery(id+"F22.wireOp",EDGE,"E80"),sQuery(id+"F22.wireOp",EDGE,"E81")])]});
            var Q1;
            Q1=qCreatedBy(makeId("Front.planeOp"),FACE);
            mirror(context, id + "F24", {"entities" : qUnion([Q0]), "mirrorPlane" : qUnion([Q1])});
        }
        {
            var Q0;
            Q0=makeQuery(id+"F17.opExtrude","SWEPT_FACE",FACE,{"disambiguationData":[OSD([sQuery(id+"F16.wireOp",EDGE,"E65")])]});
            var sketch = newSketch(context, id + "F25", { "sketchPlane" : qUnion([Q0])});
            skLineSegment(sketch, "E83", {"start": v(-146, -46) * mm, "end": v(-130, -46) * mm});
            skLineSegment(sketch, "E84", {"start": v(-130, -46) * mm, "end": v(-130, -43) * mm});
            skLineSegment(sketch, "E85", {"start": v(-130, -43) * mm, "end": v(-143, -43) * mm});
            skLineSegment(sketch, "E86", {"start": v(-143, -43) * mm, "end": v(-143, -30) * mm});
            skLineSegment(sketch, "E87", {"start": v(-143, -30) * mm, "end": v(-146, -30) * mm});
            skLineSegment(sketch, "E88", {"start": v(-146, -30) * mm, "end": v(-146, -46) * mm});
            skSolve(sketch);
        }
        {
            var Q0;
            Q0 = qSketchRegion(id + "F25", true);
            var Q1;
            Q1=makeQuery(id+"F19.opPattern","COPY",FACE,{"derivedFrom":makeQuery(id+"F17.opExtrude","SWEPT_FACE",FACE,{"disambiguationData":[OSD([sQuery(id+"F16.wireOp",EDGE,"E65")])]}),"instanceName":"1"});
            extrude(context, id + "F26", {"entities" : qUnion([Q0]), "endBound" : BoundingType.UP_TO_SURFACE, "endBoundEntityFace" : qUnion([Q1]), "depth" : 25 * mm});
        }
        {
            var Q0;
            Q0=makeQuery(id+"F26.opExtrude","SWEPT_BODY",BODY,{"disambiguationData":[OSD([sQuery(id+"F25.wireOp",EDGE,"E83"),sQuery(id+"F25.wireOp",EDGE,"E84"),sQuery(id+"F25.wireOp",EDGE,"E85"),sQuery(id+"F25.wireOp",EDGE,"E86"),sQuery(id+"F25.wireOp",EDGE,"E87"),sQuery(id+"F25.wireOp",EDGE,"E88")])]});
            var Q1;
            Q1=qCreatedBy(makeId("Front.planeOp"),FACE);
            mirror(context, id + "F27", {"entities" : qUnion([Q0]), "mirrorPlane" : qUnion([Q1])});
        }
        {
            var Q0;
            Q0=makeQuery(id+"F9.opPattern","COPY",FACE,{"derivedFrom":makeQuery(id+"F8.opExtrude","CAP_FACE",FACE,{"disambiguationData":[OSD([sQuery(id+"F7.wireOp",EDGE,"E21.0"),sQuery(id+"F7.wireOp",EDGE,"E21.1"),sQuery(id+"F7.wireOp",EDGE,"E23"),sQuery(id+"F7.wireOp",EDGE,"E24"),sQuery(id+"F7.wireOp",EDGE,"E25"),sQuery(id+"F7.wireOp",EDGE,"E26"),sQuery(id+"F7.wireOp",EDGE,"E27.filletArc"),sQuery(id+"F7.wireOp",EDGE,"E28.filletArc"),sQuery(id+"F7.wireOp",EDGE,"E29.MirrorCS"),sQuery(id+"F7.wireOp",EDGE,"E30.MirrorCS"),sQuery(id+"F7.wireOp",EDGE,"E31.MirrorCS"),sQuery(id+"F7.wireOp",EDGE,"E33.MirrorCS"),sQuery(id+"F7.wireOp",EDGE,"E34.MirrorCS"),sQuery(id+"F7.wireOp",EDGE,"E35.MirrorCS"),sQuery(id+"F7.wireOp",EDGE,"E36.MirrorCS"),sQuery(id+"F7.wireOp",EDGE,"4e9f4d0c-7754-498c-804e-4cfdb606c8ca8.MirrorCS")])],"isStart":true}),"instanceName":"1"});
            var sketch = newSketch(context, id + "F28", { "sketchPlane" : qUnion([Q0])});
            skLineSegment(sketch, "E89.bottom", {"start": v(-133, 3.4) * mm, "end": v(-105.7, 3.4) * mm});
            skLineSegment(sketch, "E89.top", {"start": v(-133, -28) * mm, "end": v(-105.7, -28) * mm});
            skLineSegment(sketch, "E89.left", {"start": v(-133, 3.4) * mm, "end": v(-133, -28) * mm});
            skLineSegment(sketch, "E89.right", {"start": v(-105.7, 3.4) * mm, "end": v(-105.7, -28) * mm});
            skLineSegment(sketch, "E90", {"start": v(-133, -12.3) * mm, "end": v(-105.7, -12.3) * mm, "construction": true});
            skCircle(sketch, "E91", {"center": v(-137.35, -12.3) * mm, "radius": 1.75 * mm});
            skCircle(sketch, "E92", {"center": v(-101.35, -12.3) * mm, "radius": 1.75 * mm});
            skLineSegment(sketch, "E93", {"start": v(-119.35, 3.4) * mm, "end": v(-119.35, -28) * mm, "construction": true});
            skLineSegment(sketch, "E94.bottom", {"start": v(-175.4, 1.35) * mm, "end": v(-153, 1.35) * mm});
            skLineSegment(sketch, "E94.top", {"start": v(-175.4, -25.95) * mm, "end": v(-153, -25.95) * mm});
            skLineSegment(sketch, "E94.left", {"start": v(-175.4, 1.35) * mm, "end": v(-175.4, -25.95) * mm});
            skLineSegment(sketch, "E94.right", {"start": v(-153, 1.35) * mm, "end": v(-153, -25.95) * mm});
            skSolve(sketch);
        }
        {
            var Q0;
            Q0 = qSketchRegion(id + "F28", true);
            extrude(context, id + "F29", {"entities" : qUnion([Q0]), "operationType" : NewBodyOperationType.REMOVE, "endBound" : BoundingType.UP_TO_NEXT, "oppositeDirection" : true, "depth" : 25 * mm});
        }
        {
            var Q0;
            Q0=makeQuery(id+"F17.opExtrude","SWEPT_FACE",FACE,{"disambiguationData":[OSD([sQuery(id+"F16.wireOp",EDGE,"E62")])]});
            var sketch = newSketch(context, id + "F30", { "sketchPlane" : qUnion([Q0])});
            skLineSegment(sketch, "E95", {"start": v(193, 75) * mm, "end": v(177, 75) * mm});
            skPoint(sketch, "E95.endSnap0", {"position": v(191.5, 75) * mm});
            skLineSegment(sketch, "E96", {"start": v(177, 75) * mm, "end": v(177, 72) * mm});
            skLineSegment(sketch, "E97", {"start": v(177, 72) * mm, "end": v(190, 72) * mm});
            skLineSegment(sketch, "E98", {"start": v(190, 72) * mm, "end": v(190, 59) * mm});
            skLineSegment(sketch, "E99", {"start": v(190, 59) * mm, "end": v(193, 59) * mm});
            skLineSegment(sketch, "E100", {"start": v(193, 59) * mm, "end": v(193, 75) * mm});
            skSolve(sketch);
        }
        {
            var Q0;
            Q0 = qSketchRegion(id + "F30", true);
            var Q1;
            Q1=makeQuery(id+"F18.opPattern","COPY",FACE,{"derivedFrom":makeQuery(id+"F17.opExtrude","SWEPT_FACE",FACE,{"disambiguationData":[OSD([sQuery(id+"F16.wireOp",EDGE,"E62")])]}),"instanceName":"1"});
            extrude(context, id + "F31", {"entities" : qUnion([Q0]), "endBound" : BoundingType.UP_TO_SURFACE, "endBoundEntityFace" : qUnion([Q1]), "depth" : 25 * mm});
        }
        {
            var Q0;
            Q0=makeQuery(id+"F31.opExtrude","SWEPT_BODY",BODY,{"disambiguationData":[OSD([sQuery(id+"F30.wireOp",EDGE,"E95"),sQuery(id+"F30.wireOp",EDGE,"E96"),sQuery(id+"F30.wireOp",EDGE,"E97"),sQuery(id+"F30.wireOp",EDGE,"E98"),sQuery(id+"F30.wireOp",EDGE,"E99"),sQuery(id+"F30.wireOp",EDGE,"E100")])]});
            var Q1;
            Q1=qCreatedBy(makeId("Right.planeOp"),FACE);
            mirror(context, id + "F32", {"entities" : qUnion([Q0]), "mirrorPlane" : qUnion([Q1])});
        }
        {
            var Q0;
            Q0=makeQuery(id+"F17.opExtrude","SWEPT_FACE",FACE,{"disambiguationData":[OSD([sQuery(id+"F16.wireOp",EDGE,"E62")])]});
            var sketch = newSketch(context, id + "F33", { "sketchPlane" : qUnion([Q0])});
            skLineSegment(sketch, "E101", {"start": v(193, -46) * mm, "end": v(177, -46) * mm});
            skLineSegment(sketch, "E102", {"start": v(177, -46) * mm, "end": v(177, -43) * mm});
            skLineSegment(sketch, "E103", {"start": v(177, -43) * mm, "end": v(190, -43) * mm});
            skLineSegment(sketch, "E104", {"start": v(190, -43) * mm, "end": v(190, -30) * mm});
            skLineSegment(sketch, "E105", {"start": v(190, -30) * mm, "end": v(193, -30) * mm});
            skLineSegment(sketch, "E106", {"start": v(193, -30) * mm, "end": v(193, -46) * mm});
            skSolve(sketch);
        }
        {
            var Q0;
            Q0 = qSketchRegion(id + "F33", true);
            var Q1;
            Q1=makeQuery(id+"F18.opPattern","COPY",FACE,{"derivedFrom":makeQuery(id+"F17.opExtrude","SWEPT_FACE",FACE,{"disambiguationData":[OSD([sQuery(id+"F16.wireOp",EDGE,"E62")])]}),"instanceName":"1"});
            extrude(context, id + "F34", {"entities" : qUnion([Q0]), "endBound" : BoundingType.UP_TO_SURFACE, "endBoundEntityFace" : qUnion([Q1]), "depth" : 25 * mm});
        }
        {
            var Q0;
            Q0=makeQuery(id+"F34.opExtrude","SWEPT_BODY",BODY,{"disambiguationData":[OSD([sQuery(id+"F33.wireOp",EDGE,"E101"),sQuery(id+"F33.wireOp",EDGE,"E102"),sQuery(id+"F33.wireOp",EDGE,"E103"),sQuery(id+"F33.wireOp",EDGE,"E104"),sQuery(id+"F33.wireOp",EDGE,"E105"),sQuery(id+"F33.wireOp",EDGE,"E106")])]});
            var Q1;
            Q1=qCreatedBy(makeId("Right.planeOp"),FACE);
            mirror(context, id + "F35", {"entities" : qUnion([Q0]), "mirrorPlane" : qUnion([Q1])});
        }
        {
            var Q0;
            Q0=makeQuery(id+"F9.opPattern","COPY",FACE,{"derivedFrom":makeQuery(id+"F8.opExtrude","CAP_FACE",FACE,{"disambiguationData":[OSD([sQuery(id+"F7.wireOp",EDGE,"E21.0"),sQuery(id+"F7.wireOp",EDGE,"E21.1"),sQuery(id+"F7.wireOp",EDGE,"E23"),sQuery(id+"F7.wireOp",EDGE,"E24"),sQuery(id+"F7.wireOp",EDGE,"E25"),sQuery(id+"F7.wireOp",EDGE,"E26"),sQuery(id+"F7.wireOp",EDGE,"E27.filletArc"),sQuery(id+"F7.wireOp",EDGE,"E28.filletArc"),sQuery(id+"F7.wireOp",EDGE,"E29.MirrorCS"),sQuery(id+"F7.wireOp",EDGE,"E30.MirrorCS"),sQuery(id+"F7.wireOp",EDGE,"E31.MirrorCS"),sQuery(id+"F7.wireOp",EDGE,"E33.MirrorCS"),sQuery(id+"F7.wireOp",EDGE,"E34.MirrorCS"),sQuery(id+"F7.wireOp",EDGE,"E35.MirrorCS"),sQuery(id+"F7.wireOp",EDGE,"E36.MirrorCS"),sQuery(id+"F7.wireOp",EDGE,"4e9f4d0c-7754-498c-804e-4cfdb606c8ca8.MirrorCS")])],"isStart":true}),"instanceName":"1"});
            var sketch = newSketch(context, id + "F36", { "sketchPlane" : qUnion([Q0])});
            skLineSegment(sketch, "E107.bottom", {"start": v(-20, 55) * mm, "end": v(20, 55) * mm});
            skLineSegment(sketch, "E107.top", {"start": v(-20, 49) * mm, "end": v(20, 49) * mm});
            skLineSegment(sketch, "E108", {"start": v(0, 0) * mm, "end": v(0, 75) * mm, "construction": true});
            skArc(sketch, "E109", {"start": v(-20, 55) * mm, "mid": v(-23, 52) * mm, "end": v(-20, 49) * mm});
            skArc(sketch, "E110", {"start": v(20, 55) * mm, "mid": v(23, 52) * mm, "end": v(20, 49) * mm});
            skLineSegment(sketch, "E111", {"start": v(20, 52) * mm, "end": v(48.86, 52) * mm, "construction": true});
            skPoint(sketch, "E111.endSnap0", {"position": v(23, 52) * mm});
            skLineSegment(sketch, "E112.1.0.0", {"start": v(48, 49) * mm, "end": v(88, 49) * mm});
            skPoint(sketch, "E112.1.0.1", {"position": v(91, 52) * mm});
            skLineSegment(sketch, "E112.1.0.2", {"start": v(48, 55) * mm, "end": v(88, 55) * mm});
            skLineSegment(sketch, "E112.1.0.3", {"start": v(88, 52) * mm, "end": v(116.86, 52) * mm, "construction": true});
            skArc(sketch, "E112.1.0.4", {"start": v(48, 55) * mm, "mid": v(45, 52) * mm, "end": v(48, 49) * mm});
            skArc(sketch, "E112.1.0.5", {"start": v(88, 55) * mm, "mid": v(91, 52) * mm, "end": v(88, 49) * mm});
            skLineSegment(sketch, "E112.2.0.0", {"start": v(116, 49) * mm, "end": v(156, 49) * mm});
            skPoint(sketch, "E112.2.0.1", {"position": v(159, 52) * mm});
            skLineSegment(sketch, "E112.2.0.2", {"start": v(116, 55) * mm, "end": v(156, 55) * mm});
            skLineSegment(sketch, "E112.2.0.3", {"start": v(156, 52) * mm, "end": v(184.86, 52) * mm, "construction": true});
            skArc(sketch, "E112.2.0.4", {"start": v(116, 55) * mm, "mid": v(113, 52) * mm, "end": v(116, 49) * mm});
            skArc(sketch, "E112.2.0.5", {"start": v(156, 55) * mm, "mid": v(159, 52) * mm, "end": v(156, 49) * mm});
            skLineSegment(sketch, "E112.direction1", {"start": v(-20, 49) * mm, "end": v(48, 49) * mm, "construction": true});
            skPoint(sketch, "E113.MirrorP", {"position": v(-159, 52) * mm});
            skLineSegment(sketch, "E114.MirrorCS", {"start": v(-116, 55) * mm, "end": v(-156, 55) * mm});
            skLineSegment(sketch, "E115.MirrorCS", {"start": v(-116, 49) * mm, "end": v(-156, 49) * mm});
            skArc(sketch, "E116.MirrorCS", {"start": v(-116, 55) * mm, "mid": v(-113, 52) * mm, "end": v(-116, 49) * mm});
            skArc(sketch, "E117.MirrorCS", {"start": v(-156, 55) * mm, "mid": v(-159, 52) * mm, "end": v(-156, 49) * mm});
            skArc(sketch, "E118.MirrorCS", {"start": v(-88, 55) * mm, "mid": v(-91, 52) * mm, "end": v(-88, 49) * mm});
            skArc(sketch, "E119.MirrorCS", {"start": v(-48, 55) * mm, "mid": v(-45, 52) * mm, "end": v(-48, 49) * mm});
            skLineSegment(sketch, "E120.MirrorCS", {"start": v(-48, 55) * mm, "end": v(-88, 55) * mm});
            skLineSegment(sketch, "E121.MirrorCS", {"start": v(-48, 49) * mm, "end": v(-88, 49) * mm});
            skPoint(sketch, "E122.MirrorP", {"position": v(-91, 52) * mm});
            skSolve(sketch);
        }
        {
            var Q0;
            Q0 = qSketchRegion(id + "F36", true);
            extrude(context, id + "F37", {"entities" : qUnion([Q0]), "operationType" : NewBodyOperationType.REMOVE, "endBound" : BoundingType.UP_TO_NEXT, "oppositeDirection" : true, "depth" : 25 * mm});
        }
        {
            var Q0;
            Q0=makeQuery(id+"F15.opExtrude","SWEPT_BODY",BODY,{"disambiguationData":[OSD([sQuery(id+"F14.wireOp",EDGE,"E59.bottom"),sQuery(id+"F14.wireOp",EDGE,"E59.top"),sQuery(id+"F14.wireOp",EDGE,"E59.left"),sQuery(id+"F14.wireOp",EDGE,"E59.right")])]});
            var Q1;
            Q1=qCreatedBy(makeId("Right.planeOp"),FACE);
            mirror(context, id + "F38", {"entities" : qUnion([Q0]), "mirrorPlane" : qUnion([Q1])});
        }
    });
